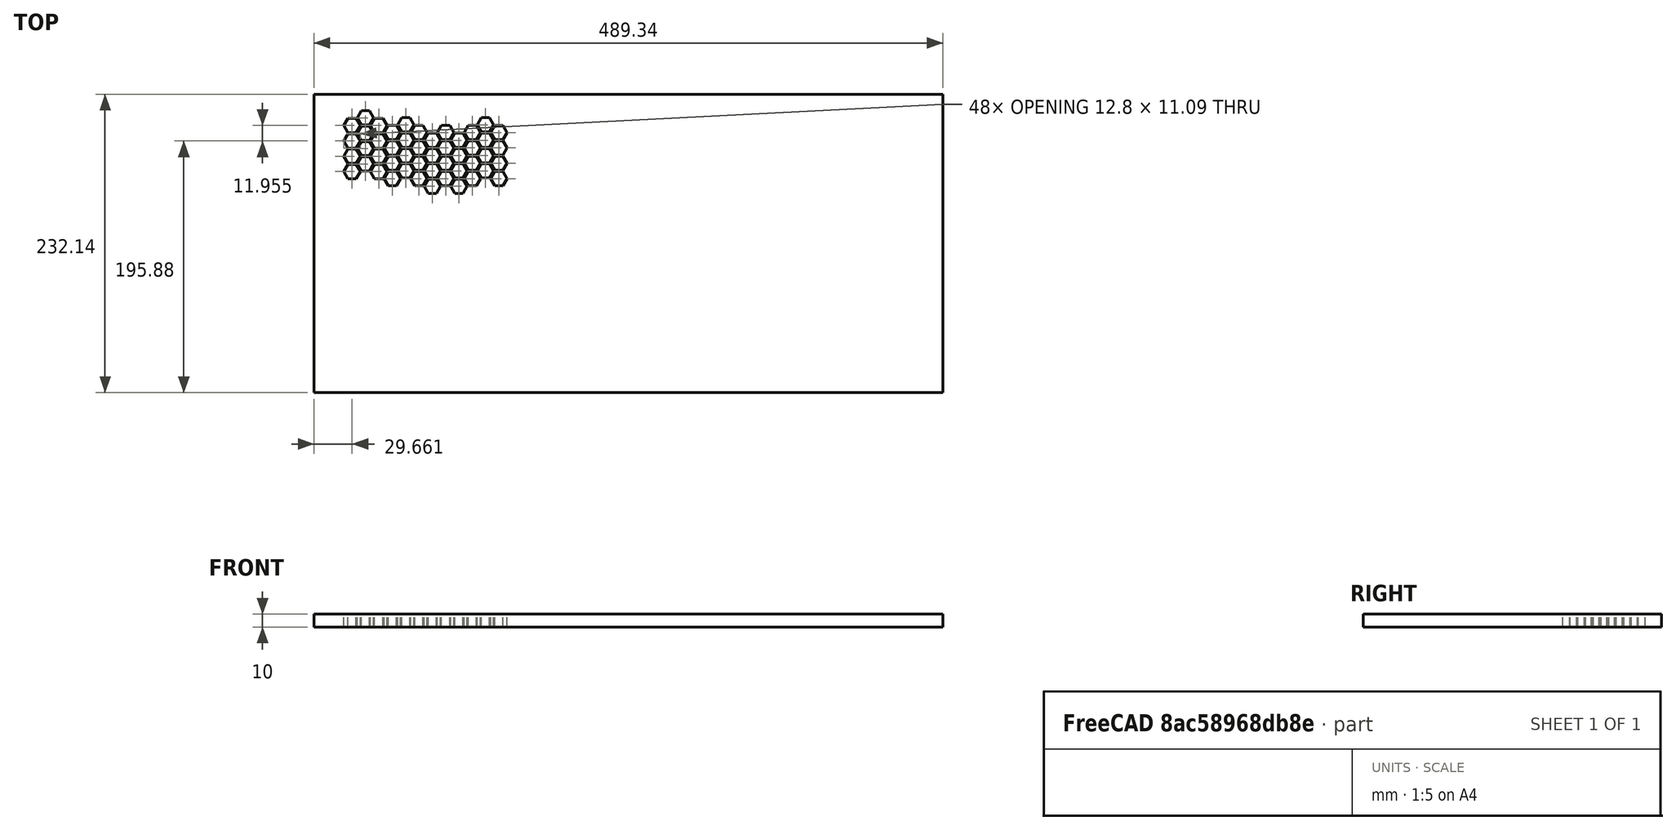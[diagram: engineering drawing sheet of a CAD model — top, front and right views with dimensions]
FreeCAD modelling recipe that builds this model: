
FCSTD DOCUMENT  (FreeCAD 0.21R33771 (Git))
Label: voshina
License: All rights reserved
LicenseURL: http://en.wikipedia.org/wiki/All_rights_reserved
objects: Sketcher::SketchObject×1, PartDesign::Pad×1, PartDesign::Body×1
note: 4 computed .brp shape members not serialized (recipe doc carries the construction recipe); baked Part::Feature solids carry a one-line shape summary decoded from their .brp

FEATURE [Sketcher::SketchObject] Sketch
  FullyConstrained = false
  MapMode = 5
  Support = -> [XY_Plane]
  sketch-geometry (437):
    g0: LineSegment StartX=-244.671 StartY=116.069 StartZ=0 EndX=-244.671 EndY=-116.069 EndZ=0
    g1: LineSegment StartX=-244.671 StartY=-116.069 StartZ=0 EndX=244.671 EndY=-116.069 EndZ=0
    g2: LineSegment StartX=244.671 StartY=-116.069 StartZ=0 EndX=244.671 EndY=116.069 EndZ=0
    g3: LineSegment StartX=244.671 StartY=116.069 StartZ=0 EndX=-244.671 EndY=116.069 EndZ=0
    g4: GeomPoint X=0 Y=0 Z=0
    g5: LineSegment StartX=-211.809 StartY=86.2231 StartZ=0 EndX=-208.609 EndY=91.7656 EndZ=0
    g6: LineSegment StartX=-208.609 StartY=91.7656 StartZ=0 EndX=-211.809 EndY=97.3082 EndZ=0
    g7: LineSegment StartX=-211.809 StartY=97.3082 StartZ=0 EndX=-218.209 EndY=97.3082 EndZ=0
    g8: LineSegment StartX=-218.209 StartY=97.3082 StartZ=0 EndX=-221.409 EndY=91.7656 EndZ=0
    g9: LineSegment StartX=-221.409 StartY=91.7656 StartZ=0 EndX=-218.209 EndY=86.2231 EndZ=0
    g10: LineSegment StartX=-218.209 StartY=86.2231 StartZ=0 EndX=-211.809 EndY=86.2231 EndZ=0
    g11: Circle CenterX=-215.009 CenterY=91.7656 CenterZ=0 NormalX=0 NormalY=0 NormalZ=1 AngleXU=0 Radius=6.4
    g12: LineSegment StartX=-187.902 StartY=91.7656 StartZ=0 EndX=-191.102 EndY=97.3082 EndZ=0
    g13: LineSegment StartX=-191.102 StartY=97.3082 StartZ=0 EndX=-197.502 EndY=97.3082 EndZ=0
    g14: LineSegment StartX=-197.502 StartY=97.3082 StartZ=0 EndX=-200.702 EndY=91.7656 EndZ=0
    g15: LineSegment StartX=-200.702 StartY=91.7656 StartZ=0 EndX=-197.502 EndY=86.2231 EndZ=0
    g16: LineSegment StartX=-197.502 StartY=86.2231 StartZ=0 EndX=-191.102 EndY=86.2231 EndZ=0
    g17: LineSegment StartX=-191.102 StartY=86.2231 StartZ=0 EndX=-187.902 EndY=91.7656 EndZ=0
    g18: Circle CenterX=-194.302 CenterY=91.7656 CenterZ=0 NormalX=0 NormalY=0 NormalZ=1 AngleXU=0 Radius=6.4
    g19: LineSegment StartX=-198.255 StartY=97.7432 StartZ=0 EndX=-201.455 EndY=103.286 EndZ=0
    g20: LineSegment StartX=-201.455 StartY=103.286 StartZ=0 EndX=-207.855 EndY=103.286 EndZ=0
    g21: LineSegment StartX=-207.855 StartY=103.286 StartZ=0 EndX=-211.055 EndY=97.7432 EndZ=0
    g22: LineSegment StartX=-211.055 StartY=97.7432 StartZ=0 EndX=-207.855 EndY=92.2006 EndZ=0
    g23: LineSegment StartX=-207.855 StartY=92.2006 StartZ=0 EndX=-201.455 EndY=92.2006 EndZ=0
    g24: LineSegment StartX=-201.455 StartY=92.2006 StartZ=0 EndX=-198.255 EndY=97.7432 EndZ=0
    g25: Circle CenterX=-204.655 CenterY=97.7432 CenterZ=0 NormalX=0 NormalY=0 NormalZ=1 AngleXU=0 Radius=6.4
    g26: LineSegment StartX=-211.809 StartY=74.2679 StartZ=0 EndX=-208.609 EndY=79.8105 EndZ=0
    g27: LineSegment StartX=-208.609 StartY=79.8105 StartZ=0 EndX=-211.809 EndY=85.3531 EndZ=0
    g28: LineSegment StartX=-211.809 StartY=85.3531 StartZ=0 EndX=-218.209 EndY=85.3531 EndZ=0
    g29: LineSegment StartX=-218.209 StartY=85.3531 StartZ=0 EndX=-221.409 EndY=79.8105 EndZ=0
    g30: LineSegment StartX=-221.409 StartY=79.8105 StartZ=0 EndX=-218.209 EndY=74.2679 EndZ=0
    g31: LineSegment StartX=-218.209 StartY=74.2679 StartZ=0 EndX=-211.809 EndY=74.2679 EndZ=0
    g32: Circle CenterX=-215.009 CenterY=79.8105 CenterZ=0 NormalX=0 NormalY=0 NormalZ=1 AngleXU=0 Radius=6.4
    g33: LineSegment StartX=-187.902 StartY=79.8105 StartZ=0 EndX=-191.102 EndY=85.3531 EndZ=0
    g34: LineSegment StartX=-191.102 StartY=85.3531 StartZ=0 EndX=-197.502 EndY=85.3531 EndZ=0
    g35: LineSegment StartX=-197.502 StartY=85.3531 StartZ=0 EndX=-200.702 EndY=79.8105 EndZ=0
    g36: LineSegment StartX=-200.702 StartY=79.8105 StartZ=0 EndX=-197.502 EndY=74.2679 EndZ=0
    g37: LineSegment StartX=-197.502 StartY=74.2679 StartZ=0 EndX=-191.102 EndY=74.2679 EndZ=0
    g38: LineSegment StartX=-191.102 StartY=74.2679 StartZ=0 EndX=-187.902 EndY=79.8105 EndZ=0
    g39: Circle CenterX=-194.302 CenterY=79.8105 CenterZ=0 NormalX=0 NormalY=0 NormalZ=1 AngleXU=0 Radius=6.4
    g40: LineSegment StartX=-198.255 StartY=85.7881 StartZ=0 EndX=-201.455 EndY=91.3306 EndZ=0
    g41: LineSegment StartX=-201.455 StartY=91.3306 StartZ=0 EndX=-207.855 EndY=91.3306 EndZ=0
    g42: LineSegment StartX=-207.855 StartY=91.3306 StartZ=0 EndX=-211.055 EndY=85.7881 EndZ=0
    g43: LineSegment StartX=-211.055 StartY=85.7881 StartZ=0 EndX=-207.855 EndY=80.2455 EndZ=0
    g44: LineSegment StartX=-207.855 StartY=80.2455 StartZ=0 EndX=-201.455 EndY=80.2455 EndZ=0
    g45: LineSegment StartX=-201.455 StartY=80.2455 StartZ=0 EndX=-198.255 EndY=85.7881 EndZ=0
    g46: Circle CenterX=-204.655 CenterY=85.7881 CenterZ=0 NormalX=0 NormalY=0 NormalZ=1 AngleXU=0 Radius=6.4
    g47: LineSegment StartX=-207.855 StartY=92.2006 StartZ=0 EndX=-208.609 EndY=91.7656 EndZ=0
    g48: LineSegment StartX=-208.609 StartY=91.7656 StartZ=0 EndX=-207.855 EndY=91.3306 EndZ=0
    g49: LineSegment StartX=-207.855 StartY=91.3306 StartZ=0 EndX=-207.855 EndY=92.2006 EndZ=0
    g50: LineSegment StartX=-201.455 StartY=92.2006 StartZ=0 EndX=-200.702 EndY=91.7656 EndZ=0
    g51: LineSegment StartX=-200.702 StartY=91.7656 StartZ=0 EndX=-201.455 EndY=91.3306 EndZ=0
    g52: LineSegment StartX=-201.455 StartY=91.3306 StartZ=0 EndX=-201.455 EndY=92.2006 EndZ=0
    g53: LineSegment StartX=-211.809 StartY=86.2231 StartZ=0 EndX=-211.809 EndY=85.3531 EndZ=0
    g54: LineSegment StartX=-211.809 StartY=85.3531 StartZ=0 EndX=-211.055 EndY=85.7881 EndZ=0
    g55: LineSegment StartX=-211.055 StartY=85.7881 StartZ=0 EndX=-211.809 EndY=86.2231 EndZ=0
    g56: LineSegment StartX=-198.255 StartY=85.7881 StartZ=0 EndX=-197.502 EndY=86.2231 EndZ=0
    g57: LineSegment StartX=-197.502 StartY=86.2231 StartZ=0 EndX=-197.502 EndY=85.3531 EndZ=0
    g58: LineSegment StartX=-197.502 StartY=85.3531 StartZ=0 EndX=-198.255 EndY=85.7881 EndZ=0
    g59: LineSegment StartX=-211.806 StartY=62.3079 StartZ=0 EndX=-208.606 EndY=67.8505 EndZ=0
    g60: LineSegment StartX=-208.606 StartY=67.8505 StartZ=0 EndX=-211.806 EndY=73.3931 EndZ=0
    g61: LineSegment StartX=-211.806 StartY=73.3931 StartZ=0 EndX=-218.206 EndY=73.3931 EndZ=0
    g62: LineSegment StartX=-218.206 StartY=73.3931 StartZ=0 EndX=-221.406 EndY=67.8505 EndZ=0
    g63: LineSegment StartX=-221.406 StartY=67.8505 StartZ=0 EndX=-218.206 EndY=62.3079 EndZ=0
    g64: LineSegment StartX=-218.206 StartY=62.3079 StartZ=0 EndX=-211.806 EndY=62.3079 EndZ=0
    g65: Circle CenterX=-215.006 CenterY=67.8505 CenterZ=0 NormalX=0 NormalY=0 NormalZ=1 AngleXU=0 Radius=6.4
    g66: LineSegment StartX=-187.899 StartY=67.8505 StartZ=0 EndX=-191.099 EndY=73.3931 EndZ=0
    g67: LineSegment StartX=-191.099 StartY=73.3931 StartZ=0 EndX=-197.499 EndY=73.3931 EndZ=0
    g68: LineSegment StartX=-197.499 StartY=73.3931 StartZ=0 EndX=-200.699 EndY=67.8505 EndZ=0
    g69: LineSegment StartX=-200.699 StartY=67.8505 StartZ=0 EndX=-197.499 EndY=62.3079 EndZ=0
    g70: LineSegment StartX=-197.499 StartY=62.3079 StartZ=0 EndX=-191.099 EndY=62.3079 EndZ=0
    g71: LineSegment StartX=-191.099 StartY=62.3079 StartZ=0 EndX=-187.899 EndY=67.8505 EndZ=0
    g72: Circle CenterX=-194.299 CenterY=67.8505 CenterZ=0 NormalX=0 NormalY=0 NormalZ=1 AngleXU=0 Radius=6.4
    g73: LineSegment StartX=-198.253 StartY=73.8281 StartZ=0 EndX=-201.453 EndY=79.3706 EndZ=0
    g74: LineSegment StartX=-201.453 StartY=79.3706 StartZ=0 EndX=-207.853 EndY=79.3706 EndZ=0
    g75: LineSegment StartX=-207.853 StartY=79.3706 StartZ=0 EndX=-211.053 EndY=73.8281 EndZ=0
    g76: LineSegment StartX=-211.053 StartY=73.8281 StartZ=0 EndX=-207.853 EndY=68.2855 EndZ=0
    g77: LineSegment StartX=-207.853 StartY=68.2855 StartZ=0 EndX=-201.453 EndY=68.2855 EndZ=0
    g78: LineSegment StartX=-201.453 StartY=68.2855 StartZ=0 EndX=-198.253 EndY=73.8281 EndZ=0
    g79: Circle CenterX=-204.653 CenterY=73.8281 CenterZ=0 NormalX=0 NormalY=0 NormalZ=1 AngleXU=0 Radius=6.4
    g80: LineSegment StartX=-211.806 StartY=50.3528 StartZ=0 EndX=-208.606 EndY=55.8954 EndZ=0
    g81: LineSegment StartX=-208.606 StartY=55.8954 StartZ=0 EndX=-211.806 EndY=61.4379 EndZ=0
    g82: LineSegment StartX=-211.806 StartY=61.4379 StartZ=0 EndX=-218.206 EndY=61.4379 EndZ=0
    g83: LineSegment StartX=-218.206 StartY=61.4379 StartZ=0 EndX=-221.406 EndY=55.8954 EndZ=0
    g84: LineSegment StartX=-221.406 StartY=55.8954 StartZ=0 EndX=-218.206 EndY=50.3528 EndZ=0
    g85: LineSegment StartX=-218.206 StartY=50.3528 StartZ=0 EndX=-211.806 EndY=50.3528 EndZ=0
    g86: Circle CenterX=-215.006 CenterY=55.8954 CenterZ=0 NormalX=0 NormalY=0 NormalZ=1 AngleXU=0 Radius=6.4
    g87: LineSegment StartX=-187.899 StartY=55.8954 StartZ=0 EndX=-191.099 EndY=61.4379 EndZ=0
    g88: LineSegment StartX=-191.099 StartY=61.4379 StartZ=0 EndX=-197.499 EndY=61.4379 EndZ=0
    g89: LineSegment StartX=-197.499 StartY=61.4379 StartZ=0 EndX=-200.699 EndY=55.8954 EndZ=0
    g90: LineSegment StartX=-200.699 StartY=55.8954 StartZ=0 EndX=-197.499 EndY=50.3528 EndZ=0
    g91: LineSegment StartX=-197.499 StartY=50.3528 StartZ=0 EndX=-191.099 EndY=50.3528 EndZ=0
    g92: LineSegment StartX=-191.099 StartY=50.3528 StartZ=0 EndX=-187.899 EndY=55.8954 EndZ=0
    g93: Circle CenterX=-194.299 CenterY=55.8954 CenterZ=0 NormalX=0 NormalY=0 NormalZ=1 AngleXU=0 Radius=6.4
    g94: LineSegment StartX=-198.253 StartY=61.8729 StartZ=0 EndX=-201.453 EndY=67.4155 EndZ=0
    g95: LineSegment StartX=-201.453 StartY=67.4155 StartZ=0 EndX=-207.853 EndY=67.4155 EndZ=0
    g96: LineSegment StartX=-207.853 StartY=67.4155 StartZ=0 EndX=-211.053 EndY=61.8729 EndZ=0
    g97: LineSegment StartX=-211.053 StartY=61.8729 StartZ=0 EndX=-207.853 EndY=56.3304 EndZ=0
    g98: LineSegment StartX=-207.853 StartY=56.3304 StartZ=0 EndX=-201.453 EndY=56.3304 EndZ=0
    g99: LineSegment StartX=-201.453 StartY=56.3304 StartZ=0 EndX=-198.253 EndY=61.8729 EndZ=0
    g100: Circle CenterX=-204.653 CenterY=61.8729 CenterZ=0 NormalX=0 NormalY=0 NormalZ=1 AngleXU=0 Radius=6.4
    g101: LineSegment StartX=-207.853 StartY=68.2855 StartZ=0 EndX=-208.606 EndY=67.8505 EndZ=0
    g102: LineSegment StartX=-208.606 StartY=67.8505 StartZ=0 EndX=-207.853 EndY=67.4155 EndZ=0
    g103: LineSegment StartX=-207.853 StartY=67.4155 StartZ=0 EndX=-207.853 EndY=68.2855 EndZ=0
    g104: LineSegment StartX=-201.453 StartY=68.2855 StartZ=0 EndX=-200.699 EndY=67.8505 EndZ=0
    g105: LineSegment StartX=-200.699 StartY=67.8505 StartZ=0 EndX=-201.453 EndY=67.4155 EndZ=0
    g106: LineSegment StartX=-201.453 StartY=67.4155 StartZ=0 EndX=-201.453 EndY=68.2855 EndZ=0
    g107: LineSegment StartX=-211.806 StartY=62.3079 StartZ=0 EndX=-211.806 EndY=61.4379 EndZ=0
    g108: LineSegment StartX=-211.806 StartY=61.4379 StartZ=0 EndX=-211.053 EndY=61.8729 EndZ=0
    g109: LineSegment StartX=-211.053 StartY=61.8729 StartZ=0 EndX=-211.806 EndY=62.3079 EndZ=0
    g110: LineSegment StartX=-198.253 StartY=61.8729 StartZ=0 EndX=-197.499 EndY=62.3079 EndZ=0
    g111: LineSegment StartX=-197.499 StartY=62.3079 StartZ=0 EndX=-197.499 EndY=61.4379 EndZ=0
    g112: LineSegment StartX=-197.499 StartY=61.4379 StartZ=0 EndX=-198.253 EndY=61.8729 EndZ=0
    g113: LineSegment StartX=-180.463 StartY=80.7595 StartZ=0 EndX=-177.263 EndY=86.302 EndZ=0
    g114: LineSegment StartX=-177.263 StartY=86.302 StartZ=0 EndX=-180.463 EndY=91.8446 EndZ=0
    g115: LineSegment StartX=-180.463 StartY=91.8446 StartZ=0 EndX=-186.863 EndY=91.8446 EndZ=0
    g116: LineSegment StartX=-186.863 StartY=91.8446 StartZ=0 EndX=-190.063 EndY=86.302 EndZ=0
    g117: LineSegment StartX=-190.063 StartY=86.302 StartZ=0 EndX=-186.863 EndY=80.7595 EndZ=0
    g118: LineSegment StartX=-186.863 StartY=80.7595 StartZ=0 EndX=-180.463 EndY=80.7595 EndZ=0
    g119: Circle CenterX=-183.663 CenterY=86.302 CenterZ=0 NormalX=0 NormalY=0 NormalZ=1 AngleXU=0 Radius=6.4
    g120: LineSegment StartX=-156.556 StartY=86.302 StartZ=0 EndX=-159.756 EndY=91.8446 EndZ=0
    g121: LineSegment StartX=-159.756 StartY=91.8446 StartZ=0 EndX=-166.156 EndY=91.8446 EndZ=0
    g122: LineSegment StartX=-166.156 StartY=91.8446 StartZ=0 EndX=-169.356 EndY=86.302 EndZ=0
    g123: LineSegment StartX=-169.356 StartY=86.302 StartZ=0 EndX=-166.156 EndY=80.7595 EndZ=0
    g124: LineSegment StartX=-166.156 StartY=80.7595 StartZ=0 EndX=-159.756 EndY=80.7595 EndZ=0
    g125: LineSegment StartX=-159.756 StartY=80.7595 StartZ=0 EndX=-156.556 EndY=86.302 EndZ=0
    g126: Circle CenterX=-162.956 CenterY=86.302 CenterZ=0 NormalX=0 NormalY=0 NormalZ=1 AngleXU=0 Radius=6.4
    g127: LineSegment StartX=-166.909 StartY=92.2796 StartZ=0 EndX=-170.109 EndY=97.8222 EndZ=0
    g128: LineSegment StartX=-170.109 StartY=97.8222 StartZ=0 EndX=-176.509 EndY=97.8222 EndZ=0
    g129: LineSegment StartX=-176.509 StartY=97.8222 StartZ=0 EndX=-179.709 EndY=92.2796 EndZ=0
    g130: LineSegment StartX=-179.709 StartY=92.2796 StartZ=0 EndX=-176.509 EndY=86.737 EndZ=0
    g131: LineSegment StartX=-176.509 StartY=86.737 StartZ=0 EndX=-170.109 EndY=86.737 EndZ=0
    g132: LineSegment StartX=-170.109 StartY=86.737 StartZ=0 EndX=-166.909 EndY=92.2796 EndZ=0
    g133: Circle CenterX=-173.309 CenterY=92.2796 CenterZ=0 NormalX=0 NormalY=0 NormalZ=1 AngleXU=0 Radius=6.4
    g134: LineSegment StartX=-180.463 StartY=68.8043 StartZ=0 EndX=-177.263 EndY=74.3469 EndZ=0
    g135: LineSegment StartX=-177.263 StartY=74.3469 StartZ=0 EndX=-180.463 EndY=79.8895 EndZ=0
    g136: LineSegment StartX=-180.463 StartY=79.8895 StartZ=0 EndX=-186.863 EndY=79.8895 EndZ=0
    g137: LineSegment StartX=-186.863 StartY=79.8895 StartZ=0 EndX=-190.063 EndY=74.3469 EndZ=0
    g138: LineSegment StartX=-190.063 StartY=74.3469 StartZ=0 EndX=-186.863 EndY=68.8043 EndZ=0
    g139: LineSegment StartX=-186.863 StartY=68.8043 StartZ=0 EndX=-180.463 EndY=68.8043 EndZ=0
    g140: Circle CenterX=-183.663 CenterY=74.3469 CenterZ=0 NormalX=0 NormalY=0 NormalZ=1 AngleXU=0 Radius=6.4
    g141: LineSegment StartX=-156.556 StartY=74.3469 StartZ=0 EndX=-159.756 EndY=79.8895 EndZ=0
    g142: LineSegment StartX=-159.756 StartY=79.8895 StartZ=0 EndX=-166.156 EndY=79.8895 EndZ=0
    g143: LineSegment StartX=-166.156 StartY=79.8895 StartZ=0 EndX=-169.356 EndY=74.3469 EndZ=0
    g144: LineSegment StartX=-169.356 StartY=74.3469 StartZ=0 EndX=-166.156 EndY=68.8043 EndZ=0
    g145: LineSegment StartX=-166.156 StartY=68.8043 StartZ=0 EndX=-159.756 EndY=68.8043 EndZ=0
    g146: LineSegment StartX=-159.756 StartY=68.8043 StartZ=0 EndX=-156.556 EndY=74.3469 EndZ=0
    g147: Circle CenterX=-162.956 CenterY=74.3469 CenterZ=0 NormalX=0 NormalY=0 NormalZ=1 AngleXU=0 Radius=6.4
    g148: LineSegment StartX=-166.909 StartY=80.3245 StartZ=0 EndX=-170.109 EndY=85.867 EndZ=0
    g149: LineSegment StartX=-170.109 StartY=85.867 StartZ=0 EndX=-176.509 EndY=85.867 EndZ=0
    g150: LineSegment StartX=-176.509 StartY=85.867 StartZ=0 EndX=-179.709 EndY=80.3245 EndZ=0
    g151: LineSegment StartX=-179.709 StartY=80.3245 StartZ=0 EndX=-176.509 EndY=74.7819 EndZ=0
    g152: LineSegment StartX=-176.509 StartY=74.7819 StartZ=0 EndX=-170.109 EndY=74.7819 EndZ=0
    g153: LineSegment StartX=-170.109 StartY=74.7819 StartZ=0 EndX=-166.909 EndY=80.3245 EndZ=0
    g154: Circle CenterX=-173.309 CenterY=80.3245 CenterZ=0 NormalX=0 NormalY=0 NormalZ=1 AngleXU=0 Radius=6.4
    g155: LineSegment StartX=-176.509 StartY=86.737 StartZ=0 EndX=-177.263 EndY=86.302 EndZ=0
    g156: LineSegment StartX=-177.263 StartY=86.302 StartZ=0 EndX=-176.509 EndY=85.867 EndZ=0
    g157: LineSegment StartX=-176.509 StartY=85.867 StartZ=0 EndX=-176.509 EndY=86.737 EndZ=0
    g158: LineSegment StartX=-170.109 StartY=86.737 StartZ=0 EndX=-169.356 EndY=86.302 EndZ=0
    g159: LineSegment StartX=-169.356 StartY=86.302 StartZ=0 EndX=-170.109 EndY=85.867 EndZ=0
    g160: LineSegment StartX=-170.109 StartY=85.867 StartZ=0 EndX=-170.109 EndY=86.737 EndZ=0
    g161: LineSegment StartX=-180.463 StartY=80.7595 StartZ=0 EndX=-180.463 EndY=79.8895 EndZ=0
    g162: LineSegment StartX=-180.463 StartY=79.8895 StartZ=0 EndX=-179.709 EndY=80.3245 EndZ=0
    g163: LineSegment StartX=-179.709 StartY=80.3245 StartZ=0 EndX=-180.463 EndY=80.7595 EndZ=0
    g164: LineSegment StartX=-166.909 StartY=80.3245 StartZ=0 EndX=-166.156 EndY=80.7595 EndZ=0
    g165: LineSegment StartX=-166.156 StartY=80.7595 StartZ=0 EndX=-166.156 EndY=79.8895 EndZ=0
    g166: LineSegment StartX=-166.156 StartY=79.8895 StartZ=0 EndX=-166.909 EndY=80.3245 EndZ=0
    g167: LineSegment StartX=-180.46 StartY=56.8443 StartZ=0 EndX=-177.26 EndY=62.3869 EndZ=0
    g168: LineSegment StartX=-177.26 StartY=62.3869 StartZ=0 EndX=-180.46 EndY=67.9295 EndZ=0
    g169: LineSegment StartX=-180.46 StartY=67.9295 StartZ=0 EndX=-186.86 EndY=67.9295 EndZ=0
    g170: LineSegment StartX=-186.86 StartY=67.9295 StartZ=0 EndX=-190.06 EndY=62.3869 EndZ=0
    g171: LineSegment StartX=-190.06 StartY=62.3869 StartZ=0 EndX=-186.86 EndY=56.8443 EndZ=0
    g172: LineSegment StartX=-186.86 StartY=56.8443 StartZ=0 EndX=-180.46 EndY=56.8443 EndZ=0
    g173: Circle CenterX=-183.66 CenterY=62.3869 CenterZ=0 NormalX=0 NormalY=0 NormalZ=1 AngleXU=0 Radius=6.4
    g174: LineSegment StartX=-156.553 StartY=62.3869 StartZ=0 EndX=-159.753 EndY=67.9295 EndZ=0
    g175: LineSegment StartX=-159.753 StartY=67.9295 StartZ=0 EndX=-166.153 EndY=67.9295 EndZ=0
    g176: LineSegment StartX=-166.153 StartY=67.9295 StartZ=0 EndX=-169.353 EndY=62.3869 EndZ=0
    g177: LineSegment StartX=-169.353 StartY=62.3869 StartZ=0 EndX=-166.153 EndY=56.8443 EndZ=0
    g178: LineSegment StartX=-166.153 StartY=56.8443 StartZ=0 EndX=-159.753 EndY=56.8443 EndZ=0
    g179: LineSegment StartX=-159.753 StartY=56.8443 StartZ=0 EndX=-156.553 EndY=62.3869 EndZ=0
    g180: Circle CenterX=-162.953 CenterY=62.3869 CenterZ=0 NormalX=0 NormalY=0 NormalZ=1 AngleXU=0 Radius=6.4
    g181: LineSegment StartX=-166.907 StartY=68.3645 StartZ=0 EndX=-170.107 EndY=73.907 EndZ=0
    g182: LineSegment StartX=-170.107 StartY=73.907 StartZ=0 EndX=-176.507 EndY=73.907 EndZ=0
    g183: LineSegment StartX=-176.507 StartY=73.907 StartZ=0 EndX=-179.707 EndY=68.3645 EndZ=0
    g184: LineSegment StartX=-179.707 StartY=68.3645 StartZ=0 EndX=-176.507 EndY=62.8219 EndZ=0
    g185: LineSegment StartX=-176.507 StartY=62.8219 StartZ=0 EndX=-170.107 EndY=62.8219 EndZ=0
    g186: LineSegment StartX=-170.107 StartY=62.8219 StartZ=0 EndX=-166.907 EndY=68.3645 EndZ=0
    g187: Circle CenterX=-173.307 CenterY=68.3645 CenterZ=0 NormalX=0 NormalY=0 NormalZ=1 AngleXU=0 Radius=6.4
    g188: LineSegment StartX=-180.46 StartY=44.8892 StartZ=0 EndX=-177.26 EndY=50.4318 EndZ=0
    g189: LineSegment StartX=-177.26 StartY=50.4318 StartZ=0 EndX=-180.46 EndY=55.9743 EndZ=0
    g190: LineSegment StartX=-180.46 StartY=55.9743 StartZ=0 EndX=-186.86 EndY=55.9743 EndZ=0
    g191: LineSegment StartX=-186.86 StartY=55.9743 StartZ=0 EndX=-190.06 EndY=50.4318 EndZ=0
    g192: LineSegment StartX=-190.06 StartY=50.4318 StartZ=0 EndX=-186.86 EndY=44.8892 EndZ=0
    g193: LineSegment StartX=-186.86 StartY=44.8892 StartZ=0 EndX=-180.46 EndY=44.8892 EndZ=0
    g194: Circle CenterX=-183.66 CenterY=50.4318 CenterZ=0 NormalX=0 NormalY=0 NormalZ=1 AngleXU=0 Radius=6.4
    g195: LineSegment StartX=-156.553 StartY=50.4318 StartZ=0 EndX=-159.753 EndY=55.9743 EndZ=0
    g196: LineSegment StartX=-159.753 StartY=55.9743 StartZ=0 EndX=-166.153 EndY=55.9743 EndZ=0
    g197: LineSegment StartX=-166.153 StartY=55.9743 StartZ=0 EndX=-169.353 EndY=50.4318 EndZ=0
    g198: LineSegment StartX=-169.353 StartY=50.4318 StartZ=0 EndX=-166.153 EndY=44.8892 EndZ=0
    g199: LineSegment StartX=-166.153 StartY=44.8892 StartZ=0 EndX=-159.753 EndY=44.8892 EndZ=0
    g200: LineSegment StartX=-159.753 StartY=44.8892 StartZ=0 EndX=-156.553 EndY=50.4318 EndZ=0
    g201: Circle CenterX=-162.953 CenterY=50.4318 CenterZ=0 NormalX=0 NormalY=0 NormalZ=1 AngleXU=0 Radius=6.4
    g202: LineSegment StartX=-166.907 StartY=56.4093 StartZ=0 EndX=-170.107 EndY=61.9519 EndZ=0
    g203: LineSegment StartX=-170.107 StartY=61.9519 StartZ=0 EndX=-176.507 EndY=61.9519 EndZ=0
    g204: LineSegment StartX=-176.507 StartY=61.9519 StartZ=0 EndX=-179.707 EndY=56.4093 EndZ=0
    g205: LineSegment StartX=-179.707 StartY=56.4093 StartZ=0 EndX=-176.507 EndY=50.8668 EndZ=0
    g206: LineSegment StartX=-176.507 StartY=50.8668 StartZ=0 EndX=-170.107 EndY=50.8668 EndZ=0
    g207: LineSegment StartX=-170.107 StartY=50.8668 StartZ=0 EndX=-166.907 EndY=56.4093 EndZ=0
    g208: Circle CenterX=-173.307 CenterY=56.4093 CenterZ=0 NormalX=0 NormalY=0 NormalZ=1 AngleXU=0 Radius=6.4
    g209: LineSegment StartX=-176.507 StartY=62.8219 StartZ=0 EndX=-177.26 EndY=62.3869 EndZ=0
    g210: LineSegment StartX=-177.26 StartY=62.3869 StartZ=0 EndX=-176.507 EndY=61.9519 EndZ=0
    g211: LineSegment StartX=-176.507 StartY=61.9519 StartZ=0 EndX=-176.507 EndY=62.8219 EndZ=0
    g212: LineSegment StartX=-170.107 StartY=62.8219 StartZ=0 EndX=-169.353 EndY=62.3869 EndZ=0
    g213: LineSegment StartX=-169.353 StartY=62.3869 StartZ=0 EndX=-170.107 EndY=61.9519 EndZ=0
    g214: LineSegment StartX=-170.107 StartY=61.9519 StartZ=0 EndX=-170.107 EndY=62.8219 EndZ=0
    g215: LineSegment StartX=-180.46 StartY=56.8443 StartZ=0 EndX=-180.46 EndY=55.9743 EndZ=0
    g216: LineSegment StartX=-180.46 StartY=55.9743 StartZ=0 EndX=-179.707 EndY=56.4093 EndZ=0
    g217: LineSegment StartX=-179.707 StartY=56.4093 StartZ=0 EndX=-180.46 EndY=56.8443 EndZ=0
    g218: LineSegment StartX=-166.907 StartY=56.4093 StartZ=0 EndX=-166.153 EndY=56.8443 EndZ=0
    g219: LineSegment StartX=-166.153 StartY=56.8443 StartZ=0 EndX=-166.153 EndY=55.9743 EndZ=0
    g220: LineSegment StartX=-166.153 StartY=55.9743 StartZ=0 EndX=-166.907 EndY=56.4093 EndZ=0
    g221: LineSegment StartX=-149.397 StartY=74.7819 StartZ=0 EndX=-146.197 EndY=80.3245 EndZ=0
    g222: LineSegment StartX=-146.197 StartY=80.3245 StartZ=0 EndX=-149.397 EndY=85.867 EndZ=0
    g223: LineSegment StartX=-149.397 StartY=85.867 StartZ=0 EndX=-155.797 EndY=85.867 EndZ=0
    g224: LineSegment StartX=-155.797 StartY=85.867 StartZ=0 EndX=-158.997 EndY=80.3245 EndZ=0
    g225: LineSegment StartX=-158.997 StartY=80.3245 StartZ=0 EndX=-155.797 EndY=74.7819 EndZ=0
    g226: LineSegment StartX=-155.797 StartY=74.7819 StartZ=0 EndX=-149.397 EndY=74.7819 EndZ=0
    g227: Circle CenterX=-152.597 CenterY=80.3245 CenterZ=0 NormalX=0 NormalY=0 NormalZ=1 AngleXU=0 Radius=6.4
    g228: LineSegment StartX=-125.49 StartY=80.3245 StartZ=0 EndX=-128.69 EndY=85.867 EndZ=0
    g229: LineSegment StartX=-128.69 StartY=85.867 StartZ=0 EndX=-135.09 EndY=85.867 EndZ=0
    g230: LineSegment StartX=-135.09 StartY=85.867 StartZ=0 EndX=-138.29 EndY=80.3245 EndZ=0
    g231: LineSegment StartX=-138.29 StartY=80.3245 StartZ=0 EndX=-135.09 EndY=74.7819 EndZ=0
    g232: LineSegment StartX=-135.09 StartY=74.7819 StartZ=0 EndX=-128.69 EndY=74.7819 EndZ=0
    g233: LineSegment StartX=-128.69 StartY=74.7819 StartZ=0 EndX=-125.49 EndY=80.3245 EndZ=0
    g234: Circle CenterX=-131.89 CenterY=80.3245 CenterZ=0 NormalX=0 NormalY=0 NormalZ=1 AngleXU=0 Radius=6.4
    g235: LineSegment StartX=-135.843 StartY=86.302 StartZ=0 EndX=-139.043 EndY=91.8446 EndZ=0
    g236: LineSegment StartX=-139.043 StartY=91.8446 StartZ=0 EndX=-145.443 EndY=91.8446 EndZ=0
    g237: LineSegment StartX=-145.443 StartY=91.8446 StartZ=0 EndX=-148.643 EndY=86.302 EndZ=0
    g238: LineSegment StartX=-148.643 StartY=86.302 StartZ=0 EndX=-145.443 EndY=80.7595 EndZ=0
    g239: LineSegment StartX=-145.443 StartY=80.7595 StartZ=0 EndX=-139.043 EndY=80.7595 EndZ=0
    g240: LineSegment StartX=-139.043 StartY=80.7595 StartZ=0 EndX=-135.843 EndY=86.302 EndZ=0
    g241: Circle CenterX=-142.243 CenterY=86.302 CenterZ=0 NormalX=0 NormalY=0 NormalZ=1 AngleXU=0 Radius=6.4
    g242: LineSegment StartX=-149.397 StartY=62.8268 StartZ=0 EndX=-146.197 EndY=68.3693 EndZ=0
    g243: LineSegment StartX=-146.197 StartY=68.3693 StartZ=0 EndX=-149.397 EndY=73.9119 EndZ=0
    g244: LineSegment StartX=-149.397 StartY=73.9119 StartZ=0 EndX=-155.797 EndY=73.9119 EndZ=0
    g245: LineSegment StartX=-155.797 StartY=73.9119 StartZ=0 EndX=-158.997 EndY=68.3693 EndZ=0
    g246: LineSegment StartX=-158.997 StartY=68.3693 StartZ=0 EndX=-155.797 EndY=62.8268 EndZ=0
    g247: LineSegment StartX=-155.797 StartY=62.8268 StartZ=0 EndX=-149.397 EndY=62.8268 EndZ=0
    g248: Circle CenterX=-152.597 CenterY=68.3693 CenterZ=0 NormalX=0 NormalY=0 NormalZ=1 AngleXU=0 Radius=6.4
    g249: LineSegment StartX=-125.49 StartY=68.3693 StartZ=0 EndX=-128.69 EndY=73.9119 EndZ=0
    g250: LineSegment StartX=-128.69 StartY=73.9119 StartZ=0 EndX=-135.09 EndY=73.9119 EndZ=0
    g251: LineSegment StartX=-135.09 StartY=73.9119 StartZ=0 EndX=-138.29 EndY=68.3693 EndZ=0
    g252: LineSegment StartX=-138.29 StartY=68.3693 StartZ=0 EndX=-135.09 EndY=62.8268 EndZ=0
    g253: LineSegment StartX=-135.09 StartY=62.8268 StartZ=0 EndX=-128.69 EndY=62.8268 EndZ=0
    g254: LineSegment StartX=-128.69 StartY=62.8268 StartZ=0 EndX=-125.49 EndY=68.3693 EndZ=0
    g255: Circle CenterX=-131.89 CenterY=68.3693 CenterZ=0 NormalX=0 NormalY=0 NormalZ=1 AngleXU=0 Radius=6.4
    g256: LineSegment StartX=-135.843 StartY=74.3469 StartZ=0 EndX=-139.043 EndY=79.8895 EndZ=0
    g257: LineSegment StartX=-139.043 StartY=79.8895 StartZ=0 EndX=-145.443 EndY=79.8895 EndZ=0
    g258: LineSegment StartX=-145.443 StartY=79.8895 StartZ=0 EndX=-148.643 EndY=74.3469 EndZ=0
    g259: LineSegment StartX=-148.643 StartY=74.3469 StartZ=0 EndX=-145.443 EndY=68.8043 EndZ=0
    g260: LineSegment StartX=-145.443 StartY=68.8043 StartZ=0 EndX=-139.043 EndY=68.8043 EndZ=0
    g261: LineSegment StartX=-139.043 StartY=68.8043 StartZ=0 EndX=-135.843 EndY=74.3469 EndZ=0
    g262: Circle CenterX=-142.243 CenterY=74.3469 CenterZ=0 NormalX=0 NormalY=0 NormalZ=1 AngleXU=0 Radius=6.4
    g263: LineSegment StartX=-145.443 StartY=80.7595 StartZ=0 EndX=-146.197 EndY=80.3245 EndZ=0
    g264: LineSegment StartX=-146.197 StartY=80.3245 StartZ=0 EndX=-145.443 EndY=79.8895 EndZ=0
    g265: LineSegment StartX=-145.443 StartY=79.8895 StartZ=0 EndX=-145.443 EndY=80.7595 EndZ=0
    g266: LineSegment StartX=-139.043 StartY=80.7595 StartZ=0 EndX=-138.29 EndY=80.3245 EndZ=0
    g267: LineSegment StartX=-138.29 StartY=80.3245 StartZ=0 EndX=-139.043 EndY=79.8895 EndZ=0
    g268: LineSegment StartX=-139.043 StartY=79.8895 StartZ=0 EndX=-139.043 EndY=80.7595 EndZ=0
    g269: LineSegment StartX=-149.397 StartY=74.7819 StartZ=0 EndX=-149.397 EndY=73.9119 EndZ=0
    g270: LineSegment StartX=-149.397 StartY=73.9119 StartZ=0 EndX=-148.643 EndY=74.3469 EndZ=0
    g271: LineSegment StartX=-148.643 StartY=74.3469 StartZ=0 EndX=-149.397 EndY=74.7819 EndZ=0
    g272: LineSegment StartX=-135.843 StartY=74.3469 StartZ=0 EndX=-135.09 EndY=74.7819 EndZ=0
    g273: LineSegment StartX=-135.09 StartY=74.7819 StartZ=0 EndX=-135.09 EndY=73.9119 EndZ=0
    g274: LineSegment StartX=-135.09 StartY=73.9119 StartZ=0 EndX=-135.843 EndY=74.3469 EndZ=0
    g275: LineSegment StartX=-149.394 StartY=50.8668 StartZ=0 EndX=-146.194 EndY=56.4093 EndZ=0
    g276: LineSegment StartX=-146.194 StartY=56.4093 StartZ=0 EndX=-149.394 EndY=61.9519 EndZ=0
    g277: LineSegment StartX=-149.394 StartY=61.9519 StartZ=0 EndX=-155.794 EndY=61.9519 EndZ=0
    g278: LineSegment StartX=-155.794 StartY=61.9519 StartZ=0 EndX=-158.994 EndY=56.4093 EndZ=0
    g279: LineSegment StartX=-158.994 StartY=56.4093 StartZ=0 EndX=-155.794 EndY=50.8668 EndZ=0
    g280: LineSegment StartX=-155.794 StartY=50.8668 StartZ=0 EndX=-149.394 EndY=50.8668 EndZ=0
    g281: Circle CenterX=-152.594 CenterY=56.4093 CenterZ=0 NormalX=0 NormalY=0 NormalZ=1 AngleXU=0 Radius=6.4
    g282: LineSegment StartX=-125.487 StartY=56.4093 StartZ=0 EndX=-128.687 EndY=61.9519 EndZ=0
    g283: LineSegment StartX=-128.687 StartY=61.9519 StartZ=0 EndX=-135.087 EndY=61.9519 EndZ=0
    g284: LineSegment StartX=-135.087 StartY=61.9519 StartZ=0 EndX=-138.287 EndY=56.4093 EndZ=0
    g285: LineSegment StartX=-138.287 StartY=56.4093 StartZ=0 EndX=-135.087 EndY=50.8668 EndZ=0
    g286: LineSegment StartX=-135.087 StartY=50.8668 StartZ=0 EndX=-128.687 EndY=50.8668 EndZ=0
    g287: LineSegment StartX=-128.687 StartY=50.8668 StartZ=0 EndX=-125.487 EndY=56.4093 EndZ=0
    g288: Circle CenterX=-131.887 CenterY=56.4093 CenterZ=0 NormalX=0 NormalY=0 NormalZ=1 AngleXU=0 Radius=6.4
    g289: LineSegment StartX=-135.841 StartY=62.3869 StartZ=0 EndX=-139.041 EndY=67.9295 EndZ=0
    g290: LineSegment StartX=-139.041 StartY=67.9295 StartZ=0 EndX=-145.441 EndY=67.9295 EndZ=0
    g291: LineSegment StartX=-145.441 StartY=67.9295 StartZ=0 EndX=-148.641 EndY=62.3869 EndZ=0
    g292: LineSegment StartX=-148.641 StartY=62.3869 StartZ=0 EndX=-145.441 EndY=56.8443 EndZ=0
    g293: LineSegment StartX=-145.441 StartY=56.8443 StartZ=0 EndX=-139.041 EndY=56.8443 EndZ=0
    g294: LineSegment StartX=-139.041 StartY=56.8443 StartZ=0 EndX=-135.841 EndY=62.3869 EndZ=0
    g295: Circle CenterX=-142.241 CenterY=62.3869 CenterZ=0 NormalX=0 NormalY=0 NormalZ=1 AngleXU=0 Radius=6.4
    g296: LineSegment StartX=-149.394 StartY=38.9117 StartZ=0 EndX=-146.194 EndY=44.4542 EndZ=0
    g297: LineSegment StartX=-146.194 StartY=44.4542 StartZ=0 EndX=-149.394 EndY=49.9968 EndZ=0
    g298: LineSegment StartX=-149.394 StartY=49.9968 StartZ=0 EndX=-155.794 EndY=49.9968 EndZ=0
    g299: LineSegment StartX=-155.794 StartY=49.9968 StartZ=0 EndX=-158.994 EndY=44.4542 EndZ=0
    g300: LineSegment StartX=-158.994 StartY=44.4542 StartZ=0 EndX=-155.794 EndY=38.9117 EndZ=0
    g301: LineSegment StartX=-155.794 StartY=38.9117 StartZ=0 EndX=-149.394 EndY=38.9117 EndZ=0
    g302: Circle CenterX=-152.594 CenterY=44.4542 CenterZ=0 NormalX=0 NormalY=0 NormalZ=1 AngleXU=0 Radius=6.4
    g303: LineSegment StartX=-125.487 StartY=44.4542 StartZ=0 EndX=-128.687 EndY=49.9968 EndZ=0
    g304: LineSegment StartX=-128.687 StartY=49.9968 StartZ=0 EndX=-135.087 EndY=49.9968 EndZ=0
    g305: LineSegment StartX=-135.087 StartY=49.9968 StartZ=0 EndX=-138.287 EndY=44.4542 EndZ=0
    g306: LineSegment StartX=-138.287 StartY=44.4542 StartZ=0 EndX=-135.087 EndY=38.9117 EndZ=0
    g307: LineSegment StartX=-135.087 StartY=38.9117 StartZ=0 EndX=-128.687 EndY=38.9117 EndZ=0
    g308: LineSegment StartX=-128.687 StartY=38.9117 StartZ=0 EndX=-125.487 EndY=44.4542 EndZ=0
    g309: Circle CenterX=-131.887 CenterY=44.4542 CenterZ=0 NormalX=0 NormalY=0 NormalZ=1 AngleXU=0 Radius=6.4
    g310: LineSegment StartX=-135.841 StartY=50.4318 StartZ=0 EndX=-139.041 EndY=55.9743 EndZ=0
    g311: LineSegment StartX=-139.041 StartY=55.9743 StartZ=0 EndX=-145.441 EndY=55.9743 EndZ=0
    g312: LineSegment StartX=-145.441 StartY=55.9743 StartZ=0 EndX=-148.641 EndY=50.4318 EndZ=0
    g313: LineSegment StartX=-148.641 StartY=50.4318 StartZ=0 EndX=-145.441 EndY=44.8892 EndZ=0
    g314: LineSegment StartX=-145.441 StartY=44.8892 StartZ=0 EndX=-139.041 EndY=44.8892 EndZ=0
    g315: LineSegment StartX=-139.041 StartY=44.8892 StartZ=0 EndX=-135.841 EndY=50.4318 EndZ=0
    g316: Circle CenterX=-142.241 CenterY=50.4318 CenterZ=0 NormalX=0 NormalY=0 NormalZ=1 AngleXU=0 Radius=6.4
    g317: LineSegment StartX=-145.441 StartY=56.8443 StartZ=0 EndX=-146.194 EndY=56.4093 EndZ=0
    g318: LineSegment StartX=-146.194 StartY=56.4093 StartZ=0 EndX=-145.441 EndY=55.9743 EndZ=0
    g319: LineSegment StartX=-145.441 StartY=55.9743 StartZ=0 EndX=-145.441 EndY=56.8443 EndZ=0
    g320: LineSegment StartX=-139.041 StartY=56.8443 StartZ=0 EndX=-138.287 EndY=56.4093 EndZ=0
    g321: LineSegment StartX=-138.287 StartY=56.4093 StartZ=0 EndX=-139.041 EndY=55.9743 EndZ=0
    g322: LineSegment StartX=-139.041 StartY=55.9743 StartZ=0 EndX=-139.041 EndY=56.8443 EndZ=0
    g323: LineSegment StartX=-149.394 StartY=50.8668 StartZ=0 EndX=-149.394 EndY=49.9968 EndZ=0
    g324: LineSegment StartX=-149.394 StartY=49.9968 StartZ=0 EndX=-148.641 EndY=50.4318 EndZ=0
    g325: LineSegment StartX=-148.641 StartY=50.4318 StartZ=0 EndX=-149.394 EndY=50.8668 EndZ=0
    g326: LineSegment StartX=-135.841 StartY=50.4318 StartZ=0 EndX=-135.087 EndY=50.8668 EndZ=0
    g327: LineSegment StartX=-135.087 StartY=50.8668 StartZ=0 EndX=-135.087 EndY=49.9968 EndZ=0
    g328: LineSegment StartX=-135.087 StartY=49.9968 StartZ=0 EndX=-135.841 EndY=50.4318 EndZ=0
    g329: LineSegment StartX=-118.331 StartY=80.7595 StartZ=0 EndX=-115.131 EndY=86.302 EndZ=0
    g330: LineSegment StartX=-115.131 StartY=86.302 StartZ=0 EndX=-118.331 EndY=91.8446 EndZ=0
    g331: LineSegment StartX=-118.331 StartY=91.8446 StartZ=0 EndX=-124.731 EndY=91.8446 EndZ=0
    g332: LineSegment StartX=-124.731 StartY=91.8446 StartZ=0 EndX=-127.931 EndY=86.302 EndZ=0
    g333: LineSegment StartX=-127.931 StartY=86.302 StartZ=0 EndX=-124.731 EndY=80.7595 EndZ=0
    g334: LineSegment StartX=-124.731 StartY=80.7595 StartZ=0 EndX=-118.331 EndY=80.7595 EndZ=0
    g335: Circle CenterX=-121.531 CenterY=86.302 CenterZ=0 NormalX=0 NormalY=0 NormalZ=1 AngleXU=0 Radius=6.4
    g336: LineSegment StartX=-94.4241 StartY=86.302 StartZ=0 EndX=-97.6241 EndY=91.8446 EndZ=0
    g337: LineSegment StartX=-97.6241 StartY=91.8446 StartZ=0 EndX=-104.024 EndY=91.8446 EndZ=0
    g338: LineSegment StartX=-104.024 StartY=91.8446 StartZ=0 EndX=-107.224 EndY=86.302 EndZ=0
    g339: LineSegment StartX=-107.224 StartY=86.302 StartZ=0 EndX=-104.024 EndY=80.7595 EndZ=0
    g340: LineSegment StartX=-104.024 StartY=80.7595 StartZ=0 EndX=-97.6241 EndY=80.7595 EndZ=0
    g341: LineSegment StartX=-97.6241 StartY=80.7595 StartZ=0 EndX=-94.4241 EndY=86.302 EndZ=0
    g342: Circle CenterX=-100.824 CenterY=86.302 CenterZ=0 NormalX=0 NormalY=0 NormalZ=1 AngleXU=0 Radius=6.4
    g343: LineSegment StartX=-104.777 StartY=92.2796 StartZ=0 EndX=-107.977 EndY=97.8222 EndZ=0
    g344: LineSegment StartX=-107.977 StartY=97.8222 StartZ=0 EndX=-114.377 EndY=97.8222 EndZ=0
    g345: LineSegment StartX=-114.377 StartY=97.8222 StartZ=0 EndX=-117.577 EndY=92.2796 EndZ=0
    g346: LineSegment StartX=-117.577 StartY=92.2796 StartZ=0 EndX=-114.377 EndY=86.737 EndZ=0
    g347: LineSegment StartX=-114.377 StartY=86.737 StartZ=0 EndX=-107.977 EndY=86.737 EndZ=0
    g348: LineSegment StartX=-107.977 StartY=86.737 StartZ=0 EndX=-104.777 EndY=92.2796 EndZ=0
    g349: Circle CenterX=-111.177 CenterY=92.2796 CenterZ=0 NormalX=0 NormalY=0 NormalZ=1 AngleXU=0 Radius=6.4
    g350: LineSegment StartX=-118.331 StartY=68.8043 StartZ=0 EndX=-115.131 EndY=74.3469 EndZ=0
    g351: LineSegment StartX=-115.131 StartY=74.3469 StartZ=0 EndX=-118.331 EndY=79.8895 EndZ=0
    g352: LineSegment StartX=-118.331 StartY=79.8895 StartZ=0 EndX=-124.731 EndY=79.8895 EndZ=0
    g353: LineSegment StartX=-124.731 StartY=79.8895 StartZ=0 EndX=-127.931 EndY=74.3469 EndZ=0
    g354: LineSegment StartX=-127.931 StartY=74.3469 StartZ=0 EndX=-124.731 EndY=68.8043 EndZ=0
    g355: LineSegment StartX=-124.731 StartY=68.8043 StartZ=0 EndX=-118.331 EndY=68.8043 EndZ=0
    g356: Circle CenterX=-121.531 CenterY=74.3469 CenterZ=0 NormalX=0 NormalY=0 NormalZ=1 AngleXU=0 Radius=6.4
    g357: LineSegment StartX=-94.4241 StartY=74.3469 StartZ=0 EndX=-97.6241 EndY=79.8895 EndZ=0
    g358: LineSegment StartX=-97.6241 StartY=79.8895 StartZ=0 EndX=-104.024 EndY=79.8895 EndZ=0
    g359: LineSegment StartX=-104.024 StartY=79.8895 StartZ=0 EndX=-107.224 EndY=74.3469 EndZ=0
    g360: LineSegment StartX=-107.224 StartY=74.3469 StartZ=0 EndX=-104.024 EndY=68.8043 EndZ=0
    g361: LineSegment StartX=-104.024 StartY=68.8043 StartZ=0 EndX=-97.6241 EndY=68.8043 EndZ=0
    g362: LineSegment StartX=-97.6241 StartY=68.8043 StartZ=0 EndX=-94.4241 EndY=74.3469 EndZ=0
    g363: Circle CenterX=-100.824 CenterY=74.3469 CenterZ=0 NormalX=0 NormalY=0 NormalZ=1 AngleXU=0 Radius=6.4
    g364: LineSegment StartX=-104.777 StartY=80.3245 StartZ=0 EndX=-107.977 EndY=85.867 EndZ=0
    g365: LineSegment StartX=-107.977 StartY=85.867 StartZ=0 EndX=-114.377 EndY=85.867 EndZ=0
    g366: LineSegment StartX=-114.377 StartY=85.867 StartZ=0 EndX=-117.577 EndY=80.3245 EndZ=0
    g367: LineSegment StartX=-117.577 StartY=80.3245 StartZ=0 EndX=-114.377 EndY=74.7819 EndZ=0
    g368: LineSegment StartX=-114.377 StartY=74.7819 StartZ=0 EndX=-107.977 EndY=74.7819 EndZ=0
    g369: LineSegment StartX=-107.977 StartY=74.7819 StartZ=0 EndX=-104.777 EndY=80.3245 EndZ=0
    g370: Circle CenterX=-111.177 CenterY=80.3245 CenterZ=0 NormalX=0 NormalY=0 NormalZ=1 AngleXU=0 Radius=6.4
    g371: LineSegment StartX=-114.377 StartY=86.737 StartZ=0 EndX=-115.131 EndY=86.302 EndZ=0
    g372: LineSegment StartX=-115.131 StartY=86.302 StartZ=0 EndX=-114.377 EndY=85.867 EndZ=0
    g373: LineSegment StartX=-114.377 StartY=85.867 StartZ=0 EndX=-114.377 EndY=86.737 EndZ=0
    g374: LineSegment StartX=-107.977 StartY=86.737 StartZ=0 EndX=-107.224 EndY=86.302 EndZ=0
    g375: LineSegment StartX=-107.224 StartY=86.302 StartZ=0 EndX=-107.977 EndY=85.867 EndZ=0
    g376: LineSegment StartX=-107.977 StartY=85.867 StartZ=0 EndX=-107.977 EndY=86.737 EndZ=0
    g377: LineSegment StartX=-118.331 StartY=80.7595 StartZ=0 EndX=-118.331 EndY=79.8895 EndZ=0
    g378: LineSegment StartX=-118.331 StartY=79.8895 StartZ=0 EndX=-117.577 EndY=80.3245 EndZ=0
    g379: LineSegment StartX=-117.577 StartY=80.3245 StartZ=0 EndX=-118.331 EndY=80.7595 EndZ=0
    g380: LineSegment StartX=-104.777 StartY=80.3245 StartZ=0 EndX=-104.024 EndY=80.7595 EndZ=0
    g381: LineSegment StartX=-104.024 StartY=80.7595 StartZ=0 EndX=-104.024 EndY=79.8895 EndZ=0
    g382: LineSegment StartX=-104.024 StartY=79.8895 StartZ=0 EndX=-104.777 EndY=80.3245 EndZ=0
    g383: LineSegment StartX=-118.328 StartY=56.8443 StartZ=0 EndX=-115.128 EndY=62.3869 EndZ=0
    g384: LineSegment StartX=-115.128 StartY=62.3869 StartZ=0 EndX=-118.328 EndY=67.9295 EndZ=0
    g385: LineSegment StartX=-118.328 StartY=67.9295 StartZ=0 EndX=-124.728 EndY=67.9295 EndZ=0
    g386: LineSegment StartX=-124.728 StartY=67.9295 StartZ=0 EndX=-127.928 EndY=62.3869 EndZ=0
    g387: LineSegment StartX=-127.928 StartY=62.3869 StartZ=0 EndX=-124.728 EndY=56.8443 EndZ=0
    g388: LineSegment StartX=-124.728 StartY=56.8443 StartZ=0 EndX=-118.328 EndY=56.8443 EndZ=0
    g389: Circle CenterX=-121.528 CenterY=62.3869 CenterZ=0 NormalX=0 NormalY=0 NormalZ=1 AngleXU=0 Radius=6.4
    g390: LineSegment StartX=-94.4212 StartY=62.3869 StartZ=0 EndX=-97.6212 EndY=67.9295 EndZ=0
    g391: LineSegment StartX=-97.6212 StartY=67.9295 StartZ=0 EndX=-104.021 EndY=67.9295 EndZ=0
    g392: LineSegment StartX=-104.021 StartY=67.9295 StartZ=0 EndX=-107.221 EndY=62.3869 EndZ=0
    g393: LineSegment StartX=-107.221 StartY=62.3869 StartZ=0 EndX=-104.021 EndY=56.8443 EndZ=0
    g394: LineSegment StartX=-104.021 StartY=56.8443 StartZ=0 EndX=-97.6212 EndY=56.8443 EndZ=0
    g395: LineSegment StartX=-97.6212 StartY=56.8443 StartZ=0 EndX=-94.4212 EndY=62.3869 EndZ=0
    g396: Circle CenterX=-100.821 CenterY=62.3869 CenterZ=0 NormalX=0 NormalY=0 NormalZ=1 AngleXU=0 Radius=6.4
    g397: LineSegment StartX=-104.775 StartY=68.3645 StartZ=0 EndX=-107.975 EndY=73.907 EndZ=0
    g398: LineSegment StartX=-107.975 StartY=73.907 StartZ=0 EndX=-114.375 EndY=73.907 EndZ=0
    g399: LineSegment StartX=-114.375 StartY=73.907 StartZ=0 EndX=-117.575 EndY=68.3645 EndZ=0
    ... +37 more geometry lines
  constraints (1015):
    c: Coincident(g0,g1)
    c: Coincident(g1,g2)
    c: Coincident(g2,g3)
    c: Coincident(g3,g0)
    c: Horizontal(g1)
    c: Horizontal(g3)
    c: Vertical(g0)
    c: Vertical(g2)
    c: Symmetric(g1,g0,g4)
    c: Coincident(g4,g-1)
    c: Coincident(g5,g6)
    c: Coincident(g6,g7)
    c: Coincident(g7,g8)
    c: Coincident(g8,g9)
    c: Coincident(g9,g10)
    c: Coincident(g10,g5)
    c: Equal(g5, g6-g10) x5
    c: PointOnObject(g5,g11)
    c: PointOnObject(g6,g11)
    c: PointOnObject(g7,g11)
    c: PointOnObject(g8,g11)
    c: PointOnObject(g9,g11)
    c: PointOnObject(g10,g11)
    c: Horizontal(g7)
    c: Distance(g11,g6) = 6.4
    c: Coincident(g12,g13)
    c: Coincident(g13,g14)
    c: Coincident(g14,g15)
    c: Coincident(g15,g16)
    c: Coincident(g16,g17)
    c: Coincident(g17,g12)
    c: Equal(g12, g13-g17) x5
    c: PointOnObject(g12,g18)
    c: PointOnObject(g13,g18)
    c: PointOnObject(g14,g18)
    c: PointOnObject(g15,g18)
    c: PointOnObject(g16,g18)
    c: PointOnObject(g17,g18)
    c: Distance(g18,g12) = 6.4
    c: Horizontal(g13)
    c: Coincident(g19,g20)
    c: Coincident(g20,g21)
    c: Coincident(g21,g22)
    c: Coincident(g22,g23)
    c: Coincident(g23,g24)
    c: Coincident(g24,g19)
    c: Equal(g19, g20-g24) x5
    c: PointOnObject(g19,g25)
    c: PointOnObject(g20,g25)
    c: PointOnObject(g21,g25)
    c: PointOnObject(g22,g25)
    c: PointOnObject(g23,g25)
    c: PointOnObject(g24,g25)
    c: Distance(g25,g19) = 6.4
    c: Horizontal(g20)
    c: Coincident(g26,g27)
    c: Coincident(g27,g28)
    c: Coincident(g28,g29)
    c: Coincident(g29,g30)
    c: Coincident(g30,g31)
    c: Coincident(g31,g26)
    c: Equal(g26, g27-g31) x5
    c: PointOnObject(g26,g32)
    c: PointOnObject(g27,g32)
    c: PointOnObject(g28,g32)
    c: PointOnObject(g29,g32)
    c: PointOnObject(g30,g32)
    c: PointOnObject(g31,g32)
    c: Horizontal(g28)
    c: Distance(g32,g27) = 6.4
    c: Coincident(g33,g34)
    c: Coincident(g34,g35)
    c: Coincident(g35,g36)
    c: Coincident(g36,g37)
    c: Coincident(g37,g38)
    c: Coincident(g38,g33)
    c: Equal(g33, g34-g38) x5
    c: PointOnObject(g33,g39)
    c: PointOnObject(g34,g39)
    c: PointOnObject(g35,g39)
    c: PointOnObject(g36,g39)
    c: PointOnObject(g37,g39)
    c: PointOnObject(g38,g39)
    c: Distance(g39,g33) = 6.4
    c: Horizontal(g34)
    c: Coincident(g40,g41)
    c: Coincident(g41,g42)
    c: Coincident(g42,g43)
    c: Coincident(g43,g44)
    c: Coincident(g44,g45)
    c: Coincident(g45,g40)
    c: Equal(g40, g41-g45) x5
    c: PointOnObject(g40,g46)
    c: PointOnObject(g41,g46)
    c: PointOnObject(g42,g46)
    c: PointOnObject(g43,g46)
    c: PointOnObject(g44,g46)
    c: PointOnObject(g45,g46)
    c: Distance(g46,g40) = 6.4
    c: Horizontal(g41)
    c: Coincident(g47,g22)
    c: Coincident(g47,g5)
    c: Coincident(g48,g5)
    c: Coincident(g48,g41)
    c: Coincident(g49,g41)
    c: Coincident(g49,g22)
    c: Equal(g49,g47)
    c: Equal(g48,g47)
    c: Coincident(g50,g23)
    c: Coincident(g50,g14)
    c: Coincident(g51,g14)
    c: Coincident(g51,g40)
    c: Coincident(g52,g40)
    c: Coincident(g52,g23)
    c: Vertical(g52)
    c: Equal(g52,g50)
    c: Equal(g50,g51)
    c: Coincident(g53,g5)
    c: Coincident(g53,g27)
    c: Vertical(g53)
    c: Coincident(g54,g27)
    c: Coincident(g54,g42)
    c: Coincident(g55,g42)
    c: Coincident(g55,g5)
    c: Equal(g55,g53)
    c: Coincident(g56,g40)
    c: Coincident(g56,g15)
    c: Coincident(g57,g15)
    c: Coincident(g57,g34)
    c: Coincident(g58,g34)
    c: Coincident(g58,g40)
    c: Equal(g56,g57)
    c: Equal(g57,g58)
    c: Coincident(g59,g60)
    c: Coincident(g60,g61)
    c: Coincident(g61,g62)
    c: Coincident(g62,g63)
    c: Coincident(g63,g64)
    c: Coincident(g64,g59)
    c: Equal(g59, g60-g64) x5
    c: PointOnObject(g59,g65)
    c: PointOnObject(g60,g65)
    c: PointOnObject(g61,g65)
    c: PointOnObject(g62,g65)
    c: PointOnObject(g63,g65)
    c: PointOnObject(g64,g65)
    c: Horizontal(g61)
    c: Distance(g65,g60) = 6.4
    c: Coincident(g66,g67)
    c: Coincident(g67,g68)
    c: Coincident(g68,g69)
    c: Coincident(g69,g70)
    c: Coincident(g70,g71)
    c: Coincident(g71,g66)
    c: Equal(g66, g67-g71) x5
    c: PointOnObject(g66,g72)
    c: PointOnObject(g67,g72)
    c: PointOnObject(g68,g72)
    c: PointOnObject(g69,g72)
    c: PointOnObject(g70,g72)
    c: PointOnObject(g71,g72)
    c: Distance(g72,g66) = 6.4
    c: Horizontal(g67)
    c: Coincident(g73,g74)
    c: Coincident(g74,g75)
    c: Coincident(g75,g76)
    c: Coincident(g76,g77)
    c: Coincident(g77,g78)
    c: Coincident(g78,g73)
    c: Equal(g73, g74-g78) x5
    c: PointOnObject(g73,g79)
    c: PointOnObject(g74,g79)
    c: PointOnObject(g75,g79)
    c: PointOnObject(g76,g79)
    c: PointOnObject(g77,g79)
    c: PointOnObject(g78,g79)
    c: Distance(g79,g73) = 6.4
    c: Horizontal(g74)
    c: Coincident(g80,g81)
    c: Coincident(g81,g82)
    c: Coincident(g82,g83)
    c: Coincident(g83,g84)
    c: Coincident(g84,g85)
    c: Coincident(g85,g80)
    c: Equal(g80, g81-g85) x5
    c: PointOnObject(g80,g86)
    c: PointOnObject(g81,g86)
    c: PointOnObject(g82,g86)
    c: PointOnObject(g83,g86)
    c: PointOnObject(g84,g86)
    c: PointOnObject(g85,g86)
    c: Horizontal(g82)
    c: Distance(g86,g81) = 6.4
    c: Coincident(g87,g88)
    c: Coincident(g88,g89)
    c: Coincident(g89,g90)
    c: Coincident(g90,g91)
    c: Coincident(g91,g92)
    c: Coincident(g92,g87)
    c: Equal(g87, g88-g92) x5
    c: PointOnObject(g87,g93)
    c: PointOnObject(g88,g93)
    c: PointOnObject(g89,g93)
    c: PointOnObject(g90,g93)
    c: PointOnObject(g91,g93)
    c: PointOnObject(g92,g93)
    c: Distance(g93,g87) = 6.4
    c: Horizontal(g88)
    c: Coincident(g94,g95)
    c: Coincident(g95,g96)
    c: Coincident(g96,g97)
    c: Coincident(g97,g98)
    c: Coincident(g98,g99)
    c: Coincident(g99,g94)
    c: Equal(g94, g95-g99) x5
    c: PointOnObject(g94,g100)
    c: PointOnObject(g95,g100)
    c: PointOnObject(g96,g100)
    c: PointOnObject(g97,g100)
    c: PointOnObject(g98,g100)
    c: PointOnObject(g99,g100)
    c: Distance(g100,g94) = 6.4
    c: Horizontal(g95)
    c: Coincident(g101,g76)
    c: Coincident(g101,g59)
    c: Coincident(g102,g59)
    c: Coincident(g102,g95)
    c: Coincident(g103,g95)
    c: Coincident(g103,g76)
    c: Equal(g103,g101)
    c: Equal(g102,g101)
    c: Coincident(g104,g77)
    c: Coincident(g104,g68)
    c: Coincident(g105,g68)
    c: Coincident(g105,g94)
    c: Coincident(g106,g94)
    c: Coincident(g106,g77)
    c: Vertical(g106)
    c: Equal(g106,g104)
    c: Equal(g104,g105)
    c: Coincident(g107,g59)
    c: Coincident(g107,g81)
    c: Vertical(g107)
    c: Coincident(g108,g81)
    c: Coincident(g108,g96)
    c: Coincident(g109,g96)
    c: Coincident(g109,g59)
    c: Equal(g109,g107)
    c: Coincident(g110,g94)
    c: Coincident(g110,g69)
    c: Coincident(g111,g69)
    c: Coincident(g111,g88)
    c: Coincident(g112,g88)
    c: Coincident(g112,g94)
    c: Equal(g110,g111)
    c: Equal(g111,g112)
    c: Distance(g19,g14) = 0.87
    c: Distance(g73,g67) = 0.87
    c: DistanceY(g79,g46) = 11.96
    c: Distance(g32,g79) = 11.96
    c: Coincident(g113,g114)
    c: Coincident(g114,g115)
    c: Coincident(g115,g116)
    c: Coincident(g116,g117)
    c: Coincident(g117,g118)
    c: Coincident(g118,g113)
    c: Equal(g113, g114-g118) x5
    c: PointOnObject(g113,g119)
    c: PointOnObject(g114,g119)
    c: PointOnObject(g115,g119)
    c: PointOnObject(g116,g119)
    c: PointOnObject(g117,g119)
    c: PointOnObject(g118,g119)
    c: Horizontal(g115)
    c: Distance(g119,g114) = 6.4
    c: Coincident(g120,g121)
    c: Coincident(g121,g122)
    c: Coincident(g122,g123)
    c: Coincident(g123,g124)
    c: Coincident(g124,g125)
    c: Coincident(g125,g120)
    c: Equal(g120, g121-g125) x5
    c: PointOnObject(g120,g126)
    c: PointOnObject(g121,g126)
    c: PointOnObject(g122,g126)
    c: PointOnObject(g123,g126)
    c: PointOnObject(g124,g126)
    c: PointOnObject(g125,g126)
    c: Distance(g126,g120) = 6.4
    c: Horizontal(g121)
    c: Coincident(g127,g128)
    c: Coincident(g128,g129)
    c: Coincident(g129,g130)
    c: Coincident(g130,g131)
    c: Coincident(g131,g132)
    c: Coincident(g132,g127)
    c: Equal(g127, g128-g132) x5
    c: PointOnObject(g127,g133)
    c: PointOnObject(g128,g133)
    c: PointOnObject(g129,g133)
    c: PointOnObject(g130,g133)
    c: PointOnObject(g131,g133)
    c: PointOnObject(g132,g133)
    c: Distance(g133,g127) = 6.4
    c: Horizontal(g128)
    c: Coincident(g134,g135)
    c: Coincident(g135,g136)
    c: Coincident(g136,g137)
    c: Coincident(g137,g138)
    c: Coincident(g138,g139)
    c: Coincident(g139,g134)
    c: Equal(g134, g135-g139) x5
    c: PointOnObject(g134,g140)
    c: PointOnObject(g135,g140)
    c: PointOnObject(g136,g140)
    c: PointOnObject(g137,g140)
    c: PointOnObject(g138,g140)
    c: PointOnObject(g139,g140)
    c: Horizontal(g136)
    c: Distance(g140,g135) = 6.4
    c: Coincident(g141,g142)
    c: Coincident(g142,g143)
    c: Coincident(g143,g144)
    c: Coincident(g144,g145)
    c: Coincident(g145,g146)
    c: Coincident(g146,g141)
    c: Equal(g141, g142-g146) x5
    c: PointOnObject(g141,g147)
    c: PointOnObject(g142,g147)
    c: PointOnObject(g143,g147)
    c: PointOnObject(g144,g147)
    c: PointOnObject(g145,g147)
    c: PointOnObject(g146,g147)
    c: Distance(g147,g141) = 6.4
    c: Horizontal(g142)
    c: Coincident(g148,g149)
    c: Coincident(g149,g150)
    c: Coincident(g150,g151)
    c: Coincident(g151,g152)
    c: Coincident(g152,g153)
    c: Coincident(g153,g148)
    c: Equal(g148, g149-g153) x5
    c: PointOnObject(g148,g154)
    c: PointOnObject(g149,g154)
    c: PointOnObject(g150,g154)
    c: PointOnObject(g151,g154)
    c: PointOnObject(g152,g154)
    c: PointOnObject(g153,g154)
    c: Distance(g154,g148) = 6.4
    c: Horizontal(g149)
    c: Coincident(g155,g130)
    c: Coincident(g155,g113)
    c: Coincident(g156,g113)
    c: Coincident(g156,g149)
    c: Coincident(g157,g149)
    c: Coincident(g157,g130)
    c: Equal(g157,g155)
    c: Equal(g156,g155)
    c: Coincident(g158,g131)
    c: Coincident(g158,g122)
    c: Coincident(g159,g122)
    c: Coincident(g159,g148)
    c: Coincident(g160,g148)
    c: Coincident(g160,g131)
    c: Vertical(g160)
    c: Equal(g160,g158)
    c: Equal(g158,g159)
    c: Coincident(g161,g113)
    c: Coincident(g161,g135)
    c: Vertical(g161)
    c: Coincident(g162,g135)
    c: Coincident(g162,g150)
    c: Coincident(g163,g150)
    c: Coincident(g163,g113)
    c: Equal(g163,g161)
    c: Coincident(g164,g148)
    c: Coincident(g164,g123)
    c: Coincident(g165,g123)
    c: Coincident(g165,g142)
    c: Coincident(g166,g142)
    c: Coincident(g166,g148)
    c: Equal(g164,g165)
    c: Equal(g165,g166)
    c: Coincident(g167,g168)
    c: Coincident(g168,g169)
    c: Coincident(g169,g170)
    c: Coincident(g170,g171)
    c: Coincident(g171,g172)
    c: Coincident(g172,g167)
    c: Equal(g167, g168-g172) x5
    c: PointOnObject(g167,g173)
    c: PointOnObject(g168,g173)
    c: PointOnObject(g169,g173)
    c: PointOnObject(g170,g173)
    c: PointOnObject(g171,g173)
    c: PointOnObject(g172,g173)
    c: Horizontal(g169)
    c: Distance(g173,g168) = 6.4
    c: Coincident(g174,g175)
    c: Coincident(g175,g176)
    c: Coincident(g176,g177)
    c: Coincident(g177,g178)
    c: Coincident(g178,g179)
    c: Coincident(g179,g174)
    c: Equal(g174, g175-g179) x5
    c: PointOnObject(g174,g180)
    c: PointOnObject(g175,g180)
    c: PointOnObject(g176,g180)
    c: PointOnObject(g177,g180)
    c: PointOnObject(g178,g180)
    c: PointOnObject(g179,g180)
    c: Distance(g180,g174) = 6.4
    c: Horizontal(g175)
    c: Coincident(g181,g182)
    c: Coincident(g182,g183)
    c: Coincident(g183,g184)
    c: Coincident(g184,g185)
    c: Coincident(g185,g186)
    c: Coincident(g186,g181)
    c: Equal(g181, g182-g186) x5
    c: PointOnObject(g181,g187)
    c: PointOnObject(g182,g187)
    c: PointOnObject(g183,g187)
    c: PointOnObject(g184,g187)
    c: PointOnObject(g185,g187)
    c: PointOnObject(g186,g187)
    c: Distance(g187,g181) = 6.4
    c: Horizontal(g182)
    c: Coincident(g188,g189)
    c: Coincident(g189,g190)
    c: Coincident(g190,g191)
    c: Coincident(g191,g192)
    c: Coincident(g192,g193)
    c: Coincident(g193,g188)
    c: Equal(g188, g189-g193) x5
    c: PointOnObject(g188,g194)
    c: PointOnObject(g189,g194)
    c: PointOnObject(g190,g194)
    c: PointOnObject(g191,g194)
    c: PointOnObject(g192,g194)
    c: PointOnObject(g193,g194)
    c: Horizontal(g190)
    c: Distance(g194,g189) = 6.4
    c: Coincident(g195,g196)
    c: Coincident(g196,g197)
    c: Coincident(g197,g198)
    c: Coincident(g198,g199)
    c: Coincident(g199,g200)
    c: Coincident(g200,g195)
    c: Equal(g195, g196-g200) x5
    c: PointOnObject(g195,g201)
    c: PointOnObject(g196,g201)
    c: PointOnObject(g197,g201)
    c: PointOnObject(g198,g201)
    c: PointOnObject(g199,g201)
    c: PointOnObject(g200,g201)
    c: Distance(g201,g195) = 6.4
    c: Horizontal(g196)
    c: Coincident(g202,g203)
    c: Coincident(g203,g204)
    c: Coincident(g204,g205)
    c: Coincident(g205,g206)
    c: Coincident(g206,g207)
    c: Coincident(g207,g202)
    c: Equal(g202, g203-g207) x5
    c: PointOnObject(g202,g208)
    c: PointOnObject(g203,g208)
    c: PointOnObject(g204,g208)
    c: PointOnObject(g205,g208)
    c: PointOnObject(g206,g208)
    c: PointOnObject(g207,g208)
    c: Distance(g208,g202) = 6.4
    c: Horizontal(g203)
    c: Coincident(g209,g184)
    c: Coincident(g209,g167)
    c: Coincident(g210,g167)
    c: Coincident(g210,g203)
    c: Coincident(g211,g203)
    c: Coincident(g211,g184)
    c: Equal(g211,g209)
    c: Equal(g210,g209)
    c: Coincident(g212,g185)
    c: Coincident(g212,g176)
    c: Coincident(g213,g176)
    c: Coincident(g213,g202)
    c: Coincident(g214,g202)
    c: Coincident(g214,g185)
    c: Vertical(g214)
    c: Equal(g214,g212)
    c: Equal(g212,g213)
    c: Coincident(g215,g167)
    c: Coincident(g215,g189)
    c: Vertical(g215)
    c: Coincident(g216,g189)
    c: Coincident(g216,g204)
    c: Coincident(g217,g204)
    c: Coincident(g217,g167)
    c: Equal(g217,g215)
    c: Coincident(g218,g202)
    c: Coincident(g218,g177)
    c: Coincident(g219,g177)
    c: Coincident(g219,g196)
    c: Coincident(g220,g196)
    c: Coincident(g220,g202)
    c: Equal(g218,g219)
    c: Equal(g219,g220)
    c: Distance(g127,g122) = 0.87
    c: Distance(g181,g175) = 0.87
    c: DistanceY(g187,g154) = 11.96
    c: Distance(g140,g187) = 11.96
    c: Distance(g18,g119) = 11.96
    c: Coincident(g221,g222)
    c: Coincident(g222,g223)
    c: Coincident(g223,g224)
    c: Coincident(g224,g225)
    c: Coincident(g225,g226)
    c: Coincident(g226,g221)
    c: Equal(g221, g222-g226) x5
    c: PointOnObject(g221,g227)
    c: PointOnObject(g222,g227)
    c: PointOnObject(g223,g227)
    c: PointOnObject(g224,g227)
    c: PointOnObject(g225,g227)
    c: PointOnObject(g226,g227)
    c: Horizontal(g223)
    c: Distance(g227,g222) = 6.4
    c: Coincident(g228,g229)
    c: Coincident(g229,g230)
    c: Coincident(g230,g231)
    c: Coincident(g231,g232)
    c: Coincident(g232,g233)
    c: Coincident(g233,g228)
    c: Equal(g228, g229-g233) x5
    c: PointOnObject(g228,g234)
    c: PointOnObject(g229,g234)
    c: PointOnObject(g230,g234)
    c: PointOnObject(g231,g234)
    c: PointOnObject(g232,g234)
    c: PointOnObject(g233,g234)
    c: Distance(g234,g228) = 6.4
    c: Horizontal(g229)
    c: Coincident(g235,g236)
    c: Coincident(g236,g237)
    c: Coincident(g237,g238)
    c: Coincident(g238,g239)
    c: Coincident(g239,g240)
    c: Coincident(g240,g235)
    c: Equal(g235, g236-g240) x5
    c: PointOnObject(g235,g241)
    c: PointOnObject(g236,g241)
    c: PointOnObject(g237,g241)
    c: PointOnObject(g238,g241)
    c: PointOnObject(g239,g241)
    c: PointOnObject(g240,g241)
    c: Distance(g241,g235) = 6.4
    c: Horizontal(g236)
    c: Coincident(g242,g243)
    c: Coincident(g243,g244)
    c: Coincident(g244,g245)
    c: Coincident(g245,g246)
    c: Coincident(g246,g247)
    c: Coincident(g247,g242)
    c: Equal(g242, g243-g247) x5
    c: PointOnObject(g242,g248)
    c: PointOnObject(g243,g248)
    c: PointOnObject(g244,g248)
    c: PointOnObject(g245,g248)
    c: PointOnObject(g246,g248)
    c: PointOnObject(g247,g248)
    c: Horizontal(g244)
    c: Distance(g248,g243) = 6.4
    c: Coincident(g249,g250)
    c: Coincident(g250,g251)
    c: Coincident(g251,g252)
    c: Coincident(g252,g253)
    c: Coincident(g253,g254)
    c: Coincident(g254,g249)
    c: Equal(g249, g250-g254) x5
    c: PointOnObject(g249,g255)
    c: PointOnObject(g250,g255)
    c: PointOnObject(g251,g255)
    c: PointOnObject(g252,g255)
    c: PointOnObject(g253,g255)
    c: PointOnObject(g254,g255)
    c: Distance(g255,g249) = 6.4
    c: Horizontal(g250)
    c: Coincident(g256,g257)
    c: Coincident(g257,g258)
    c: Coincident(g258,g259)
    c: Coincident(g259,g260)
    c: Coincident(g260,g261)
    c: Coincident(g261,g256)
    c: Equal(g256, g257-g261) x5
    c: PointOnObject(g256,g262)
    c: PointOnObject(g257,g262)
    c: PointOnObject(g258,g262)
    c: PointOnObject(g259,g262)
    c: PointOnObject(g260,g262)
    c: PointOnObject(g261,g262)
    c: Distance(g262,g256) = 6.4
    c: Horizontal(g257)
    c: Coincident(g263,g238)
    c: Coincident(g263,g221)
    c: Coincident(g264,g221)
    c: Coincident(g264,g257)
    c: Coincident(g265,g257)
    c: Coincident(g265,g238)
    c: Equal(g265,g263)
    c: Equal(g264,g263)
    c: Coincident(g266,g239)
    c: Coincident(g266,g230)
    c: Coincident(g267,g230)
    c: Coincident(g267,g256)
    c: Coincident(g268,g256)
    c: Coincident(g268,g239)
    c: Vertical(g268)
    c: Equal(g268,g266)
    c: Equal(g266,g267)
    c: Coincident(g269,g221)
    c: Coincident(g269,g243)
    c: Vertical(g269)
    c: Coincident(g270,g243)
    c: Coincident(g270,g258)
    c: Coincident(g271,g258)
    c: Coincident(g271,g221)
    c: Equal(g271,g269)
    c: Coincident(g272,g256)
    c: Coincident(g272,g231)
    c: Coincident(g273,g231)
    c: Coincident(g273,g250)
    c: Coincident(g274,g250)
    c: Coincident(g274,g256)
    c: Equal(g272,g273)
    c: Equal(g273,g274)
    c: Coincident(g275,g276)
    c: Coincident(g276,g277)
    c: Coincident(g277,g278)
    c: Coincident(g278,g279)
    c: Coincident(g279,g280)
    c: Coincident(g280,g275)
    c: Equal(g275, g276-g280) x5
    c: PointOnObject(g275,g281)
    c: PointOnObject(g276,g281)
    c: PointOnObject(g277,g281)
    c: PointOnObject(g278,g281)
    c: PointOnObject(g279,g281)
    c: PointOnObject(g280,g281)
    c: Horizontal(g277)
    c: Distance(g281,g276) = 6.4
    c: Coincident(g282,g283)
    c: Coincident(g283,g284)
    c: Coincident(g284,g285)
    c: Coincident(g285,g286)
    c: Coincident(g286,g287)
    c: Coincident(g287,g282)
    c: Equal(g282, g283-g287) x5
    c: PointOnObject(g282,g288)
    c: PointOnObject(g283,g288)
    c: PointOnObject(g284,g288)
    c: PointOnObject(g285,g288)
    c: PointOnObject(g286,g288)
    c: PointOnObject(g287,g288)
    c: Distance(g288,g282) = 6.4
    c: Horizontal(g283)
    c: Coincident(g289,g290)
    c: Coincident(g290,g291)
    c: Coincident(g291,g292)
    c: Coincident(g292,g293)
    c: Coincident(g293,g294)
    c: Coincident(g294,g289)
    c: Equal(g289, g290-g294) x5
    c: PointOnObject(g289,g295)
    c: PointOnObject(g290,g295)
    c: PointOnObject(g291,g295)
    c: PointOnObject(g292,g295)
    c: PointOnObject(g293,g295)
    c: PointOnObject(g294,g295)
    c: Distance(g295,g289) = 6.4
    c: Horizontal(g290)
    c: Coincident(g296,g297)
    c: Coincident(g297,g298)
    c: Coincident(g298,g299)
    c: Coincident(g299,g300)
    c: Coincident(g300,g301)
    c: Coincident(g301,g296)
    c: Equal(g296, g297-g301) x5
    c: PointOnObject(g296,g302)
    c: PointOnObject(g297,g302)
    c: PointOnObject(g298,g302)
    c: PointOnObject(g299,g302)
    c: PointOnObject(g300,g302)
    c: PointOnObject(g301,g302)
    c: Horizontal(g298)
    c: Distance(g302,g297) = 6.4
    c: Coincident(g303,g304)
    c: Coincident(g304,g305)
    c: Coincident(g305,g306)
    c: Coincident(g306,g307)
    c: Coincident(g307,g308)
    c: Coincident(g308,g303)
    c: Equal(g303, g304-g308) x5
    c: PointOnObject(g303,g309)
    c: PointOnObject(g304,g309)
    c: PointOnObject(g305,g309)
    c: PointOnObject(g306,g309)
    c: PointOnObject(g307,g309)
    c: PointOnObject(g308,g309)
    c: Distance(g309,g303) = 6.4
    c: Horizontal(g304)
    c: Coincident(g310,g311)
    c: Coincident(g311,g312)
    c: Coincident(g312,g313)
    c: Coincident(g313,g314)
    c: Coincident(g314,g315)
    c: Coincident(g315,g310)
    c: Equal(g310, g311-g315) x5
    c: PointOnObject(g310,g316)
    c: PointOnObject(g311,g316)
    c: PointOnObject(g312,g316)
    c: PointOnObject(g313,g316)
    c: PointOnObject(g314,g316)
    c: PointOnObject(g315,g316)
    c: Distance(g316,g310) = 6.4
    c: Horizontal(g311)
    c: Coincident(g317,g292)
    c: Coincident(g317,g275)
    c: Coincident(g318,g275)
    c: Coincident(g318,g311)
    c: Coincident(g319,g311)
    c: Coincident(g319,g292)
    c: Equal(g319,g317)
    c: Equal(g318,g317)
    c: Coincident(g320,g293)
    c: Coincident(g320,g284)
    c: Coincident(g321,g284)
    c: Coincident(g321,g310)
    c: Coincident(g322,g310)
    c: Coincident(g322,g293)
    c: Vertical(g322)
    c: Equal(g322,g320)
    c: Equal(g320,g321)
    c: Coincident(g323,g275)
    c: Coincident(g323,g297)
    c: Vertical(g323)
    c: Coincident(g324,g297)
    c: Coincident(g324,g312)
    c: Coincident(g325,g312)
    c: Coincident(g325,g275)
    c: Equal(g325,g323)
    c: Coincident(g326,g310)
    c: Coincident(g326,g285)
    c: Coincident(g327,g285)
    c: Coincident(g327,g304)
    c: Coincident(g328,g304)
    c: Coincident(g328,g310)
    c: Equal(g326,g327)
    c: Equal(g327,g328)
    c: Distance(g235,g230) = 0.87
    c: Distance(g289,g283) = 0.87
    c: DistanceY(g295,g262) = 11.96
    c: Distance(g248,g295) = 11.96
    c: Coincident(g329,g330)
    c: Coincident(g330,g331)
    c: Coincident(g331,g332)
    c: Coincident(g332,g333)
    c: Coincident(g333,g334)
    c: Coincident(g334,g329)
    c: Equal(g329, g330-g334) x5
    c: PointOnObject(g329,g335)
    c: PointOnObject(g330,g335)
    c: PointOnObject(g331,g335)
    c: PointOnObject(g332,g335)
    c: PointOnObject(g333,g335)
    c: PointOnObject(g334,g335)
    c: Horizontal(g331)
    c: Distance(g335,g330) = 6.4
    c: Coincident(g336,g337)
    c: Coincident(g337,g338)
    c: Coincident(g338,g339)
    c: Coincident(g339,g340)
    c: Coincident(g340,g341)
    c: Coincident(g341,g336)
    c: Equal(g336, g337-g341) x5
    c: PointOnObject(g336,g342)
    c: PointOnObject(g337,g342)
    c: PointOnObject(g338,g342)
    c: PointOnObject(g339,g342)
    c: PointOnObject(g340,g342)
    c: PointOnObject(g341,g342)
    c: Distance(g342,g336) = 6.4
    c: Horizontal(g337)
    c: Coincident(g343,g344)
    c: Coincident(g344,g345)
    c: Coincident(g345,g346)
    c: Coincident(g346,g347)
    c: Coincident(g347,g348)
    c: Coincident(g348,g343)
    c: Equal(g343, g344-g348) x5
    c: PointOnObject(g343,g349)
    c: PointOnObject(g344,g349)
    c: PointOnObject(g345,g349)
    c: PointOnObject(g346,g349)
    c: PointOnObject(g347,g349)
    c: PointOnObject(g348,g349)
    c: Distance(g349,g343) = 6.4
    c: Horizontal(g344)
    c: Coincident(g350,g351)
    c: Coincident(g351,g352)
    c: Coincident(g352,g353)
    c: Coincident(g353,g354)
    c: Coincident(g354,g355)
    c: Coincident(g355,g350)
    c: Equal(g350, g351-g355) x5
    c: PointOnObject(g350,g356)
    c: PointOnObject(g351,g356)
    c: PointOnObject(g352,g356)
    c: PointOnObject(g353,g356)
    c: PointOnObject(g354,g356)
    c: PointOnObject(g355,g356)
    c: Horizontal(g352)
    c: Distance(g356,g351) = 6.4
    c: Coincident(g357,g358)
    c: Coincident(g358,g359)
    c: Coincident(g359,g360)
    c: Coincident(g360,g361)
    c: Coincident(g361,g362)
    c: Coincident(g362,g357)
    c: Equal(g357, g358-g362) x5
    c: PointOnObject(g357,g363)
    c: PointOnObject(g358,g363)
    c: PointOnObject(g359,g363)
    c: PointOnObject(g360,g363)
    c: PointOnObject(g361,g363)
    c: PointOnObject(g362,g363)
    c: Distance(g363,g357) = 6.4
    c: Horizontal(g358)
    c: Coincident(g364,g365)
    c: Coincident(g365,g366)
    c: Coincident(g366,g367)
    c: Coincident(g367,g368)
    c: Coincident(g368,g369)
    c: Coincident(g369,g364)
    c: Equal(g364, g365-g369) x5
    c: PointOnObject(g364,g370)
    c: PointOnObject(g365,g370)
    c: PointOnObject(g366,g370)
    c: PointOnObject(g367,g370)
    c: PointOnObject(g368,g370)
    c: PointOnObject(g369,g370)
    c: Distance(g370,g364) = 6.4
    c: Horizontal(g365)
    c: Coincident(g371,g346)
    c: Coincident(g371,g329)
    c: Coincident(g372,g329)
    c: Coincident(g372,g365)
    c: Coincident(g373,g365)
    c: Coincident(g373,g346)
    c: Equal(g373,g371)
    c: Equal(g372,g371)
    c: Coincident(g374,g347)
    c: Coincident(g374,g338)
    c: Coincident(g375,g338)
    c: Coincident(g375,g364)
    c: Coincident(g376,g364)
    c: Coincident(g376,g347)
    c: Vertical(g376)
    c: Equal(g376,g374)
    c: Equal(g374,g375)
    c: Coincident(g377,g329)
    c: Coincident(g377,g351)
    c: Vertical(g377)
    c: Coincident(g378,g351)
    c: Coincident(g378,g366)
    c: Coincident(g379,g366)
    c: Coincident(g379,g329)
    c: Equal(g379,g377)
    c: Coincident(g380,g364)
    c: Coincident(g380,g339)
    c: Coincident(g381,g339)
    c: Coincident(g381,g358)
    c: Coincident(g382,g358)
    c: Coincident(g382,g364)
    c: Equal(g380,g381)
    c: Equal(g381,g382)
    c: Coincident(g383,g384)
    c: Coincident(g384,g385)
    c: Coincident(g385,g386)
    c: Coincident(g386,g387)
    c: Coincident(g387,g388)
    c: Coincident(g388,g383)
    c: Equal(g383, g384-g388) x5
    c: PointOnObject(g383,g389)
    c: PointOnObject(g384,g389)
    c: PointOnObject(g385,g389)
    c: PointOnObject(g386,g389)
    c: PointOnObject(g387,g389)
    c: PointOnObject(g388,g389)
    c: Horizontal(g385)
    c: Distance(g389,g384) = 6.4
    c: Coincident(g390,g391)
    c: Coincident(g391,g392)
    c: Coincident(g392,g393)
    c: Coincident(g393,g394)
    c: Coincident(g394,g395)
    c: Coincident(g395,g390)
    c: Equal(g390, g391-g395) x5
    c: PointOnObject(g390,g396)
    c: PointOnObject(g391,g396)
    c: PointOnObject(g392,g396)
    c: PointOnObject(g393,g396)
    c: PointOnObject(g394,g396)
    c: PointOnObject(g395,g396)
    c: Distance(g396,g390) = 6.4
    c: Horizontal(g391)
    c: Coincident(g397,g398)
    c: Coincident(g398,g399)
    c: Coincident(g399,g400)
    c: Coincident(g400,g401)
    c: Coincident(g401,g402)
    c: Coincident(g402,g397)
    c: Equal(g397, g398-g402) x5
    c: PointOnObject(g397,g403)
    c: PointOnObject(g398,g403)
    c: PointOnObject(g399,g403)
    c: PointOnObject(g400,g403)
    c: PointOnObject(g401,g403)
    c: PointOnObject(g402,g403)
    c: Distance(g403,g397) = 6.4
    c: Horizontal(g398)
    c: Coincident(g404,g405)
    c: Coincident(g405,g406)
    c: Coincident(g406,g407)
    c: Coincident(g407,g408)
    c: Coincident(g408,g409)
    c: Coincident(g409,g404)
    c: Equal(g404, g405-g409) x5
    c: PointOnObject(g404,g410)
    c: PointOnObject(g405,g410)
    c: PointOnObject(g406,g410)
    c: PointOnObject(g407,g410)
    c: PointOnObject(g408,g410)
    c: PointOnObject(g409,g410)
    c: Horizontal(g406)
    c: Distance(g410,g405) = 6.4
    c: Coincident(g411,g412)
    c: Coincident(g412,g413)
    c: Coincident(g413,g414)
    c: Coincident(g414,g415)
    c: Coincident(g415,g416)
    c: Coincident(g416,g411)
    c: Equal(g411, g412-g416) x5
    c: PointOnObject(g411,g417)
    c: PointOnObject(g412,g417)
    c: PointOnObject(g413,g417)
    c: PointOnObject(g414,g417)
    c: PointOnObject(g415,g417)
    c: PointOnObject(g416,g417)
    c: Distance(g417,g411) = 6.4
    c: Horizontal(g412)
    c: Coincident(g418,g419)
    c: Coincident(g419,g420)
    c: Coincident(g420,g421)
    c: Coincident(g421,g422)
    c: Coincident(g422,g423)
    c: Coincident(g423,g418)
    c: Equal(g418, g419-g423) x5
    c: PointOnObject(g418,g424)
    c: PointOnObject(g419,g424)
    c: PointOnObject(g420,g424)
    c: PointOnObject(g421,g424)
    c: PointOnObject(g422,g424)
    c: PointOnObject(g423,g424)
    c: Distance(g424,g418) = 6.4
    c: Horizontal(g419)
    c: Coincident(g425,g400)
    c: Coincident(g425,g383)
    c: Coincident(g426,g383)
    c: Coincident(g426,g419)
    c: Coincident(g427,g419)
    c: Coincident(g427,g400)
    c: Equal(g427,g425)
    c: Equal(g426,g425)
    c: Coincident(g428,g401)
    c: Coincident(g428,g392)
    c: Coincident(g429,g392)
    c: Coincident(g429,g418)
    c: Coincident(g430,g418)
    c: Coincident(g430,g401)
    c: Vertical(g430)
    c: Equal(g430,g428)
    c: Equal(g428,g429)
    c: Coincident(g431,g383)
    c: Coincident(g431,g405)
    c: Vertical(g431)
    c: Coincident(g432,g405)
    c: Coincident(g432,g420)
    c: Coincident(g433,g420)
    c: Coincident(g433,g383)
    c: Equal(g433,g431)
    c: Coincident(g434,g418)
    c: Coincident(g434,g393)
    c: Coincident(g435,g393)
    c: Coincident(g435,g412)
    c: Coincident(g436,g412)
    c: Coincident(g436,g418)
    c: Equal(g434,g435)
    c: Equal(g435,g436)
    c: Distance(g343,g338) = 0.87
    c: Distance(g397,g391) = 0.87
    c: DistanceY(g403,g370) = 11.96
    c: Distance(g356,g403) = 11.96
    c: Distance(g234,g335) = 11.96
    c: Distance(g126,g227) = 11.96
    c: Distance(g356,g234) = 11.96
    c: Distance(g227,g147) = 11.96
FEATURE [PartDesign::Pad] Pad
  Direction = (0,0,1)
  Length = 10
  Length2 = 10
  Profile = -> Sketch
  ReferenceAxis = -> Sketch [N_Axis]
  Refine = true
  Type = 0
FEATURE [PartDesign::Body] Body
  Group = -> [Sketch,Pad]
  Origin = -> Origin
  Tip = -> Pad
